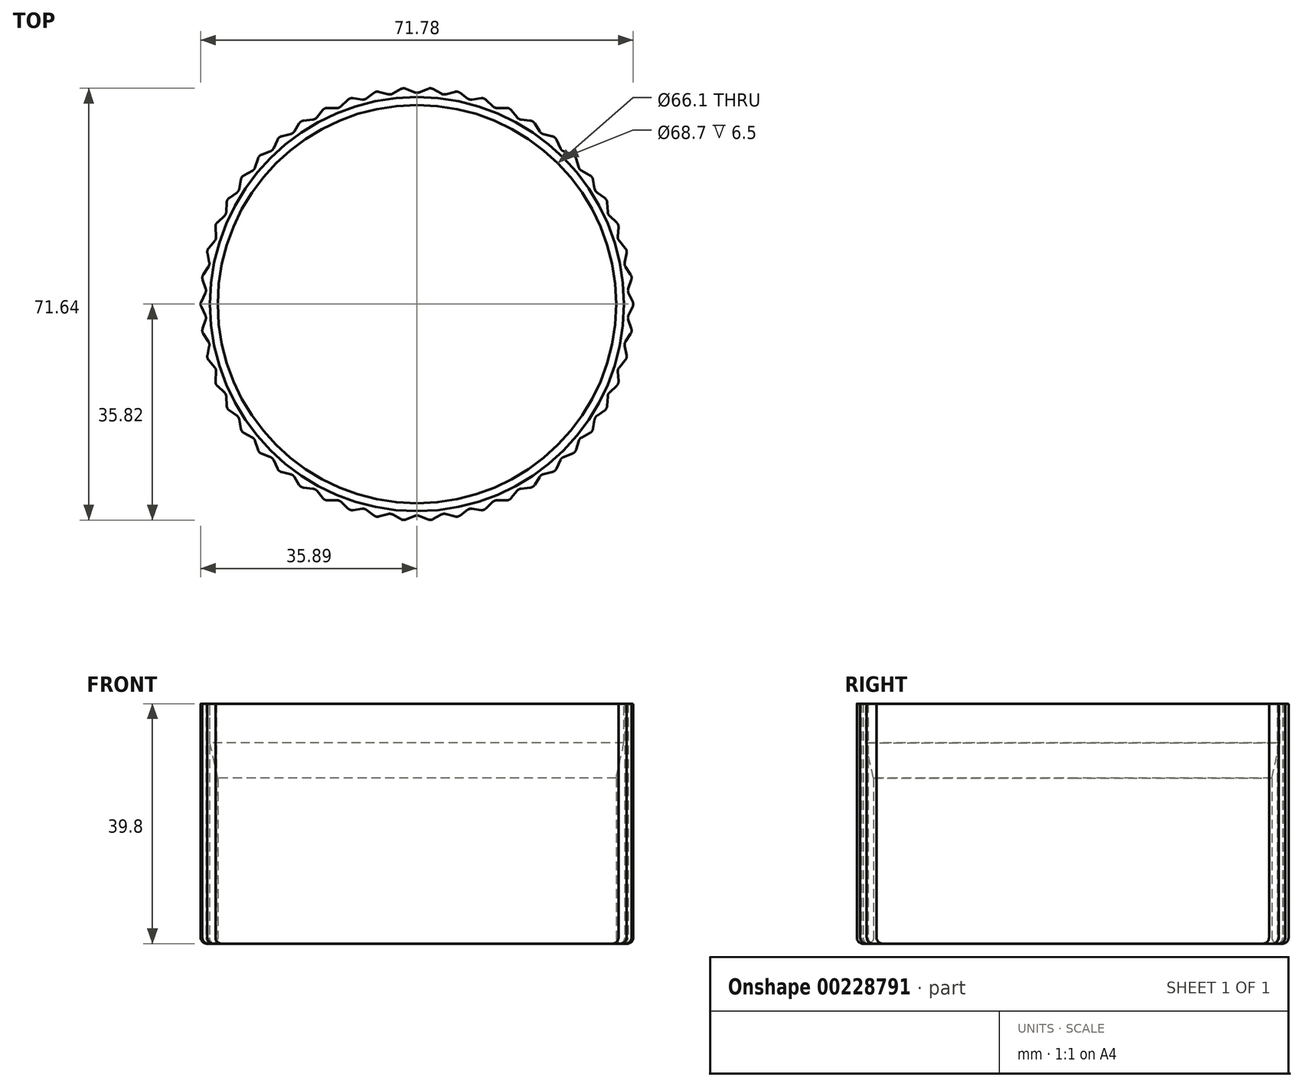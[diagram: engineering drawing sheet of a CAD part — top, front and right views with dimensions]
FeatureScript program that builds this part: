
annotation { "Feature Type Name" : "Feature", "Feature Type Description" : "" }
export const myFeature = defineFeature(function(context is Context, id is Id, definition is map)
    precondition{}
    {
        {
            var Q0;
            Q0=qCreatedBy(makeId("Top.planeOp"),FACE);
            var sketch = newSketch(context, id + "F0", { "sketchPlane" : qUnion([Q0])});
            skCircle(sketch, "E0", {"center": v(0, 0) * mm, "radius": 33.05 * mm});
            skLineSegment(sketch, "E1", {"start": v(2.68, 35.69) * mm, "end": v(4.03, 34.93) * mm});
            skLineSegment(sketch, "E2", {"start": v(4.78, 34.83) * mm, "end": v(6.28, 35.24) * mm});
            skPoint(sketch, "E3.visualSharp", {"position": v(2.26, 35.93) * mm});
            skArc(sketch, "E3.filletArc", {"start": v(2.68, 35.69) * mm, "mid": v(2.25, 35.82) * mm, "end": v(1.81, 35.74) * mm});
            skPoint(sketch, "E4.visualSharp", {"position": v(4.39, 34.72) * mm});
            skArc(sketch, "E4.filletArc", {"start": v(4.03, 34.93) * mm, "mid": v(4.4, 34.8) * mm, "end": v(4.78, 34.83) * mm});
            skPoint(sketch, "E5.visualSharp", {"position": v(6.75, 35.36) * mm});
            skArc(sketch, "E5.filletArc", {"start": v(6.72, 35.25) * mm, "mid": v(6.5, 35.27) * mm, "end": v(6.28, 35.24) * mm});
            skLineSegment(sketch, "E6.1.0", {"start": v(-1.81, 35.74) * mm, "end": v(-0.38, 35.16) * mm});
            skPoint(sketch, "E6.1.1", {"position": v(0, 35) * mm});
            skPoint(sketch, "E6.1.2", {"position": v(-2.26, 35.93) * mm});
            skArc(sketch, "E6.1.4", {"start": v(-0.38, 35.16) * mm, "mid": v(0, 35.08) * mm, "end": v(0.38, 35.16) * mm});
            skLineSegment(sketch, "E6.1.5", {"start": v(0.38, 35.16) * mm, "end": v(1.81, 35.74) * mm});
            skArc(sketch, "E6.1.6", {"start": v(-1.81, 35.74) * mm, "mid": v(-2.25, 35.82) * mm, "end": v(-2.68, 35.69) * mm});
            skArc(sketch, "E6.1.7", {"start": v(2.25, 35.82) * mm, "mid": v(2.03, 35.8) * mm, "end": v(1.81, 35.74) * mm});
            skLineSegment(sketch, "E6.2.0", {"start": v(-6.28, 35.24) * mm, "end": v(-4.78, 34.83) * mm});
            skPoint(sketch, "E6.2.1", {"position": v(-4.39, 34.72) * mm});
            skPoint(sketch, "E6.2.2", {"position": v(-6.75, 35.36) * mm});
            skPoint(sketch, "E6.2.3", {"position": v(-2.26, 35.93) * mm});
            skArc(sketch, "E6.2.4", {"start": v(-4.78, 34.83) * mm, "mid": v(-4.4, 34.8) * mm, "end": v(-4.03, 34.93) * mm});
            skLineSegment(sketch, "E6.2.5", {"start": v(-4.03, 34.93) * mm, "end": v(-2.68, 35.69) * mm});
            skArc(sketch, "E6.2.6", {"start": v(-6.28, 35.24) * mm, "mid": v(-6.72, 35.25) * mm, "end": v(-7.14, 35.07) * mm});
            skArc(sketch, "E6.2.7", {"start": v(-2.25, 35.82) * mm, "mid": v(-2.48, 35.78) * mm, "end": v(-2.68, 35.69) * mm});
            skLineSegment(sketch, "E6.3.0", {"start": v(-10.64, 34.17) * mm, "end": v(-9.11, 33.96) * mm});
            skPoint(sketch, "E6.3.1", {"position": v(-8.7, 33.9) * mm});
            skPoint(sketch, "E6.3.2", {"position": v(-11.12, 34.24) * mm});
            skPoint(sketch, "E6.3.3", {"position": v(-6.75, 35.36) * mm});
            skArc(sketch, "E6.3.4", {"start": v(-9.11, 33.96) * mm, "mid": v(-8.72, 33.98) * mm, "end": v(-8.37, 34.15) * mm});
            skLineSegment(sketch, "E6.3.5", {"start": v(-8.37, 34.15) * mm, "end": v(-7.14, 35.07) * mm});
            skArc(sketch, "E6.3.6", {"start": v(-10.64, 34.17) * mm, "mid": v(-11.09, 34.13) * mm, "end": v(-11.47, 33.9) * mm});
            skArc(sketch, "E6.3.7", {"start": v(-6.72, 35.25) * mm, "mid": v(-6.94, 35.19) * mm, "end": v(-7.14, 35.07) * mm});
            skLineSegment(sketch, "E6.4.0", {"start": v(-14.84, 32.57) * mm, "end": v(-13.3, 32.55) * mm});
            skPoint(sketch, "E6.4.1", {"position": v(-12.88, 32.54) * mm});
            skPoint(sketch, "E6.4.2", {"position": v(-15.33, 32.57) * mm});
            skPoint(sketch, "E6.4.3", {"position": v(-11.12, 34.24) * mm});
            skArc(sketch, "E6.4.4", {"start": v(-13.3, 32.55) * mm, "mid": v(-12.91, 32.62) * mm, "end": v(-12.59, 32.83) * mm});
            skLineSegment(sketch, "E6.4.5", {"start": v(-12.59, 32.83) * mm, "end": v(-11.47, 33.9) * mm});
            skArc(sketch, "E6.4.6", {"start": v(-14.84, 32.57) * mm, "mid": v(-15.28, 32.47) * mm, "end": v(-15.63, 32.2) * mm});
            skArc(sketch, "E6.4.7", {"start": v(-11.09, 34.13) * mm, "mid": v(-11.3, 34.04) * mm, "end": v(-11.47, 33.9) * mm});
            skLineSegment(sketch, "E6.5.0", {"start": v(-18.8, 30.45) * mm, "end": v(-17.27, 30.62) * mm});
            skPoint(sketch, "E6.5.1", {"position": v(-16.86, 30.67) * mm});
            skPoint(sketch, "E6.5.2", {"position": v(-19.29, 30.4) * mm});
            skPoint(sketch, "E6.5.3", {"position": v(-15.33, 32.57) * mm});
            skArc(sketch, "E6.5.4", {"start": v(-17.27, 30.62) * mm, "mid": v(-16.9, 30.74) * mm, "end": v(-16.6, 31) * mm});
            skLineSegment(sketch, "E6.5.5", {"start": v(-16.6, 31) * mm, "end": v(-15.63, 32.2) * mm});
            skArc(sketch, "E6.5.6", {"start": v(-18.8, 30.45) * mm, "mid": v(-19.23, 30.3) * mm, "end": v(-19.55, 29.98) * mm});
            skArc(sketch, "E6.5.7", {"start": v(-15.28, 32.47) * mm, "mid": v(-15.47, 32.35) * mm, "end": v(-15.63, 32.2) * mm});
            skLineSegment(sketch, "E6.6.0", {"start": v(-22.47, 27.85) * mm, "end": v(-20.97, 28.22) * mm});
            skPoint(sketch, "E6.6.1", {"position": v(-20.57, 28.32) * mm});
            skPoint(sketch, "E6.6.2", {"position": v(-22.95, 27.74) * mm});
            skPoint(sketch, "E6.6.3", {"position": v(-19.29, 30.4) * mm});
            skArc(sketch, "E6.6.4", {"start": v(-20.97, 28.22) * mm, "mid": v(-20.62, 28.38) * mm, "end": v(-20.36, 28.67) * mm});
            skLineSegment(sketch, "E6.6.5", {"start": v(-20.36, 28.67) * mm, "end": v(-19.55, 29.98) * mm});
            skArc(sketch, "E6.6.6", {"start": v(-22.47, 27.85) * mm, "mid": v(-22.88, 27.65) * mm, "end": v(-23.15, 27.3) * mm});
            skArc(sketch, "E6.6.7", {"start": v(-19.23, 30.3) * mm, "mid": v(-19.4, 30.16) * mm, "end": v(-19.55, 29.98) * mm});
            skLineSegment(sketch, "E6.7.0", {"start": v(-25.79, 24.82) * mm, "end": v(-24.34, 25.37) * mm});
            skPoint(sketch, "E6.7.1", {"position": v(-23.96, 25.51) * mm});
            skPoint(sketch, "E6.7.2", {"position": v(-26.24, 24.64) * mm});
            skPoint(sketch, "E6.7.3", {"position": v(-22.95, 27.74) * mm});
            skArc(sketch, "E6.7.4", {"start": v(-24.34, 25.37) * mm, "mid": v(-24.01, 25.57) * mm, "end": v(-23.79, 25.89) * mm});
            skLineSegment(sketch, "E6.7.5", {"start": v(-23.79, 25.89) * mm, "end": v(-23.15, 27.3) * mm});
            skArc(sketch, "E6.7.6", {"start": v(-25.79, 24.82) * mm, "mid": v(-26.16, 24.57) * mm, "end": v(-26.39, 24.18) * mm});
            skArc(sketch, "E6.7.7", {"start": v(-22.88, 27.65) * mm, "mid": v(-23.03, 27.49) * mm, "end": v(-23.15, 27.3) * mm});
            skLineSegment(sketch, "E6.8.0", {"start": v(-28.7, 21.39) * mm, "end": v(-27.33, 22.12) * mm});
            skPoint(sketch, "E6.8.1", {"position": v(-26.97, 22.3) * mm});
            skPoint(sketch, "E6.8.2", {"position": v(-29.12, 21.16) * mm});
            skPoint(sketch, "E6.8.3", {"position": v(-26.24, 24.64) * mm});
            skArc(sketch, "E6.8.4", {"start": v(-27.33, 22.12) * mm, "mid": v(-27.03, 22.36) * mm, "end": v(-26.85, 22.7) * mm});
            skLineSegment(sketch, "E6.8.5", {"start": v(-26.85, 22.7) * mm, "end": v(-26.39, 24.18) * mm});
            skArc(sketch, "E6.8.6", {"start": v(-28.7, 21.39) * mm, "mid": v(-29.03, 21.1) * mm, "end": v(-29.2, 20.68) * mm});
            skArc(sketch, "E6.8.7", {"start": v(-26.16, 24.57) * mm, "mid": v(-26.3, 24.39) * mm, "end": v(-26.39, 24.18) * mm});
            skLineSegment(sketch, "E6.9.0", {"start": v(-31.15, 17.62) * mm, "end": v(-29.89, 18.52) * mm});
            skPoint(sketch, "E6.9.1", {"position": v(-29.55, 18.75) * mm});
            skPoint(sketch, "E6.9.2", {"position": v(-31.55, 17.34) * mm});
            skPoint(sketch, "E6.9.3", {"position": v(-29.12, 21.16) * mm});
            skArc(sketch, "E6.9.4", {"start": v(-29.89, 18.52) * mm, "mid": v(-29.62, 18.8) * mm, "end": v(-29.48, 19.16) * mm});
            skLineSegment(sketch, "E6.9.5", {"start": v(-29.48, 19.16) * mm, "end": v(-29.2, 20.68) * mm});
            skArc(sketch, "E6.9.6", {"start": v(-31.15, 17.62) * mm, "mid": v(-31.45, 17.29) * mm, "end": v(-31.57, 16.86) * mm});
            skArc(sketch, "E6.9.7", {"start": v(-29.03, 21.1) * mm, "mid": v(-29.15, 20.9) * mm, "end": v(-29.2, 20.68) * mm});
            skLineSegment(sketch, "E6.10.0", {"start": v(-33.11, 13.58) * mm, "end": v(-31.97, 14.62) * mm});
            skPoint(sketch, "E6.10.1", {"position": v(-31.67, 14.9) * mm});
            skPoint(sketch, "E6.10.2", {"position": v(-33.47, 13.25) * mm});
            skPoint(sketch, "E6.10.3", {"position": v(-31.55, 17.34) * mm});
            skArc(sketch, "E6.10.4", {"start": v(-31.97, 14.62) * mm, "mid": v(-31.74, 14.94) * mm, "end": v(-31.65, 15.31) * mm});
            skLineSegment(sketch, "E6.10.5", {"start": v(-31.65, 15.31) * mm, "end": v(-31.57, 16.86) * mm});
            skArc(sketch, "E6.10.6", {"start": v(-33.11, 13.58) * mm, "mid": v(-33.37, 13.21) * mm, "end": v(-33.44, 12.77) * mm});
            skArc(sketch, "E6.10.7", {"start": v(-31.45, 17.29) * mm, "mid": v(-31.53, 17.08) * mm, "end": v(-31.57, 16.86) * mm});
            skLineSegment(sketch, "E6.11.0", {"start": v(-34.55, 9.32) * mm, "end": v(-33.55, 10.5) * mm});
            skPoint(sketch, "E6.11.1", {"position": v(-33.29, 10.82) * mm});
            skPoint(sketch, "E6.11.2", {"position": v(-34.87, 8.95) * mm});
            skPoint(sketch, "E6.11.3", {"position": v(-33.47, 13.25) * mm});
            skArc(sketch, "E6.11.4", {"start": v(-33.55, 10.5) * mm, "mid": v(-33.36, 10.84) * mm, "end": v(-33.32, 11.23) * mm});
            skLineSegment(sketch, "E6.11.5", {"start": v(-33.32, 11.23) * mm, "end": v(-33.44, 12.77) * mm});
            skArc(sketch, "E6.11.6", {"start": v(-34.55, 9.32) * mm, "mid": v(-34.76, 8.92) * mm, "end": v(-34.77, 8.48) * mm});
            skArc(sketch, "E6.11.7", {"start": v(-33.37, 13.21) * mm, "mid": v(-33.43, 13) * mm, "end": v(-33.44, 12.77) * mm});
            skLineSegment(sketch, "E6.12.0", {"start": v(-35.45, 4.92) * mm, "end": v(-34.6, 6.21) * mm});
            skPoint(sketch, "E6.12.1", {"position": v(-34.38, 6.56) * mm});
            skPoint(sketch, "E6.12.2", {"position": v(-35.72, 4.51) * mm});
            skPoint(sketch, "E6.12.3", {"position": v(-34.87, 8.95) * mm});
            skArc(sketch, "E6.12.4", {"start": v(-34.6, 6.21) * mm, "mid": v(-34.46, 6.57) * mm, "end": v(-34.46, 6.96) * mm});
            skLineSegment(sketch, "E6.12.5", {"start": v(-34.46, 6.96) * mm, "end": v(-34.77, 8.48) * mm});
            skArc(sketch, "E6.12.6", {"start": v(-35.45, 4.92) * mm, "mid": v(-35.6, 4.5) * mm, "end": v(-35.56, 4.05) * mm});
            skArc(sketch, "E6.12.7", {"start": v(-34.76, 8.92) * mm, "mid": v(-34.8, 8.7) * mm, "end": v(-34.77, 8.48) * mm});
            skLineSegment(sketch, "E6.13.0", {"start": v(-35.79, 0.44) * mm, "end": v(-35.11, 1.83) * mm});
            skPoint(sketch, "E6.13.1", {"position": v(-34.93, 2.2) * mm});
            skPoint(sketch, "E6.13.2", {"position": v(-36, 0) * mm});
            skPoint(sketch, "E6.13.3", {"position": v(-35.72, 4.51) * mm});
            skArc(sketch, "E6.13.4", {"start": v(-35.11, 1.83) * mm, "mid": v(-35.01, 2.2) * mm, "end": v(-35.06, 2.59) * mm});
            skLineSegment(sketch, "E6.13.5", {"start": v(-35.06, 2.59) * mm, "end": v(-35.56, 4.05) * mm});
            skArc(sketch, "E6.13.6", {"start": v(-35.79, 0.44) * mm, "mid": v(-35.89, 0) * mm, "end": v(-35.79, -0.44) * mm});
            skArc(sketch, "E6.13.7", {"start": v(-35.6, 4.5) * mm, "mid": v(-35.6, 4.27) * mm, "end": v(-35.56, 4.05) * mm});
            skLineSegment(sketch, "E6.14.0", {"start": v(-35.56, -4.05) * mm, "end": v(-35.06, -2.59) * mm});
            skPoint(sketch, "E6.14.1", {"position": v(-34.93, -2.2) * mm});
            skPoint(sketch, "E6.14.2", {"position": v(-35.72, -4.51) * mm});
            skPoint(sketch, "E6.14.3", {"position": v(-36, 0) * mm});
            skArc(sketch, "E6.14.4", {"start": v(-35.06, -2.59) * mm, "mid": v(-35.01, -2.2) * mm, "end": v(-35.11, -1.83) * mm});
            skLineSegment(sketch, "E6.14.5", {"start": v(-35.11, -1.83) * mm, "end": v(-35.79, -0.44) * mm});
            skArc(sketch, "E6.14.6", {"start": v(-35.56, -4.05) * mm, "mid": v(-35.6, -4.5) * mm, "end": v(-35.45, -4.92) * mm});
            skArc(sketch, "E6.14.7", {"start": v(-35.89, 0) * mm, "mid": v(-35.86, -0.22) * mm, "end": v(-35.79, -0.44) * mm});
            skLineSegment(sketch, "E6.15.0", {"start": v(-34.77, -8.48) * mm, "end": v(-34.46, -6.96) * mm});
            skPoint(sketch, "E6.15.1", {"position": v(-34.38, -6.56) * mm});
            skPoint(sketch, "E6.15.2", {"position": v(-34.87, -8.95) * mm});
            skPoint(sketch, "E6.15.3", {"position": v(-35.72, -4.51) * mm});
            skArc(sketch, "E6.15.4", {"start": v(-34.46, -6.96) * mm, "mid": v(-34.46, -6.57) * mm, "end": v(-34.6, -6.21) * mm});
            skLineSegment(sketch, "E6.15.5", {"start": v(-34.6, -6.21) * mm, "end": v(-35.45, -4.92) * mm});
            skArc(sketch, "E6.15.6", {"start": v(-34.77, -8.48) * mm, "mid": v(-34.76, -8.92) * mm, "end": v(-34.55, -9.32) * mm});
            skArc(sketch, "E6.15.7", {"start": v(-35.6, -4.5) * mm, "mid": v(-35.55, -4.72) * mm, "end": v(-35.45, -4.92) * mm});
            skLineSegment(sketch, "E6.16.0", {"start": v(-33.44, -12.77) * mm, "end": v(-33.32, -11.23) * mm});
            skPoint(sketch, "E6.16.1", {"position": v(-33.29, -10.82) * mm});
            skPoint(sketch, "E6.16.2", {"position": v(-33.47, -13.25) * mm});
            skPoint(sketch, "E6.16.3", {"position": v(-34.87, -8.95) * mm});
            skArc(sketch, "E6.16.4", {"start": v(-33.32, -11.23) * mm, "mid": v(-33.36, -10.84) * mm, "end": v(-33.55, -10.5) * mm});
            skLineSegment(sketch, "E6.16.5", {"start": v(-33.55, -10.5) * mm, "end": v(-34.55, -9.32) * mm});
            skArc(sketch, "E6.16.6", {"start": v(-33.44, -12.77) * mm, "mid": v(-33.37, -13.21) * mm, "end": v(-33.11, -13.58) * mm});
            skArc(sketch, "E6.16.7", {"start": v(-34.76, -8.92) * mm, "mid": v(-34.68, -9.14) * mm, "end": v(-34.55, -9.32) * mm});
            skLineSegment(sketch, "E6.17.0", {"start": v(-31.57, -16.86) * mm, "end": v(-31.65, -15.31) * mm});
            skPoint(sketch, "E6.17.1", {"position": v(-31.67, -14.9) * mm});
            skPoint(sketch, "E6.17.2", {"position": v(-31.55, -17.34) * mm});
            skPoint(sketch, "E6.17.3", {"position": v(-33.47, -13.25) * mm});
            skArc(sketch, "E6.17.4", {"start": v(-31.65, -15.31) * mm, "mid": v(-31.74, -14.94) * mm, "end": v(-31.97, -14.62) * mm});
            skLineSegment(sketch, "E6.17.5", {"start": v(-31.97, -14.62) * mm, "end": v(-33.11, -13.58) * mm});
            skArc(sketch, "E6.17.6", {"start": v(-31.57, -16.86) * mm, "mid": v(-31.45, -17.29) * mm, "end": v(-31.15, -17.62) * mm});
            skArc(sketch, "E6.17.7", {"start": v(-33.37, -13.21) * mm, "mid": v(-33.26, -13.41) * mm, "end": v(-33.11, -13.58) * mm});
            skLineSegment(sketch, "E6.18.0", {"start": v(-29.2, -20.68) * mm, "end": v(-29.48, -19.16) * mm});
            skPoint(sketch, "E6.18.1", {"position": v(-29.55, -18.75) * mm});
            skPoint(sketch, "E6.18.2", {"position": v(-29.12, -21.16) * mm});
            skPoint(sketch, "E6.18.3", {"position": v(-31.55, -17.34) * mm});
            skArc(sketch, "E6.18.4", {"start": v(-29.48, -19.16) * mm, "mid": v(-29.62, -18.8) * mm, "end": v(-29.89, -18.52) * mm});
            skLineSegment(sketch, "E6.18.5", {"start": v(-29.89, -18.52) * mm, "end": v(-31.15, -17.62) * mm});
            skArc(sketch, "E6.18.6", {"start": v(-29.2, -20.68) * mm, "mid": v(-29.03, -21.1) * mm, "end": v(-28.7, -21.39) * mm});
            skArc(sketch, "E6.18.7", {"start": v(-31.45, -17.29) * mm, "mid": v(-31.32, -17.47) * mm, "end": v(-31.15, -17.62) * mm});
            skLineSegment(sketch, "E6.19.0", {"start": v(-26.39, -24.18) * mm, "end": v(-26.85, -22.7) * mm});
            skPoint(sketch, "E6.19.1", {"position": v(-26.97, -22.3) * mm});
            skPoint(sketch, "E6.19.2", {"position": v(-26.24, -24.64) * mm});
            skPoint(sketch, "E6.19.3", {"position": v(-29.12, -21.16) * mm});
            skArc(sketch, "E6.19.4", {"start": v(-26.85, -22.7) * mm, "mid": v(-27.03, -22.36) * mm, "end": v(-27.33, -22.12) * mm});
            skLineSegment(sketch, "E6.19.5", {"start": v(-27.33, -22.12) * mm, "end": v(-28.7, -21.39) * mm});
            skArc(sketch, "E6.19.6", {"start": v(-26.39, -24.18) * mm, "mid": v(-26.16, -24.57) * mm, "end": v(-25.79, -24.82) * mm});
            skArc(sketch, "E6.19.7", {"start": v(-29.03, -21.1) * mm, "mid": v(-28.88, -21.26) * mm, "end": v(-28.7, -21.39) * mm});
            skLineSegment(sketch, "E6.20.0", {"start": v(-23.15, -27.3) * mm, "end": v(-23.79, -25.89) * mm});
            skPoint(sketch, "E6.20.1", {"position": v(-23.96, -25.51) * mm});
            skPoint(sketch, "E6.20.2", {"position": v(-22.95, -27.74) * mm});
            skPoint(sketch, "E6.20.3", {"position": v(-26.24, -24.64) * mm});
            skArc(sketch, "E6.20.4", {"start": v(-23.79, -25.89) * mm, "mid": v(-24.01, -25.57) * mm, "end": v(-24.34, -25.37) * mm});
            skLineSegment(sketch, "E6.20.5", {"start": v(-24.34, -25.37) * mm, "end": v(-25.79, -24.82) * mm});
            skArc(sketch, "E6.20.6", {"start": v(-23.15, -27.3) * mm, "mid": v(-22.88, -27.65) * mm, "end": v(-22.47, -27.85) * mm});
            skArc(sketch, "E6.20.7", {"start": v(-26.16, -24.57) * mm, "mid": v(-25.99, -24.71) * mm, "end": v(-25.79, -24.82) * mm});
            skLineSegment(sketch, "E6.21.0", {"start": v(-19.55, -29.98) * mm, "end": v(-20.36, -28.67) * mm});
            skPoint(sketch, "E6.21.1", {"position": v(-20.57, -28.32) * mm});
            skPoint(sketch, "E6.21.2", {"position": v(-19.29, -30.4) * mm});
            skPoint(sketch, "E6.21.3", {"position": v(-22.95, -27.74) * mm});
            skArc(sketch, "E6.21.4", {"start": v(-20.36, -28.67) * mm, "mid": v(-20.62, -28.38) * mm, "end": v(-20.97, -28.22) * mm});
            skLineSegment(sketch, "E6.21.5", {"start": v(-20.97, -28.22) * mm, "end": v(-22.47, -27.85) * mm});
            skArc(sketch, "E6.21.6", {"start": v(-19.55, -29.98) * mm, "mid": v(-19.23, -30.3) * mm, "end": v(-18.8, -30.45) * mm});
            skArc(sketch, "E6.21.7", {"start": v(-22.88, -27.65) * mm, "mid": v(-22.69, -27.78) * mm, "end": v(-22.47, -27.85) * mm});
            skLineSegment(sketch, "E6.22.0", {"start": v(-15.63, -32.2) * mm, "end": v(-16.6, -31) * mm});
            skPoint(sketch, "E6.22.1", {"position": v(-16.86, -30.67) * mm});
            skPoint(sketch, "E6.22.2", {"position": v(-15.33, -32.57) * mm});
            skPoint(sketch, "E6.22.3", {"position": v(-19.29, -30.4) * mm});
            skArc(sketch, "E6.22.4", {"start": v(-16.6, -31) * mm, "mid": v(-16.9, -30.74) * mm, "end": v(-17.27, -30.62) * mm});
            skLineSegment(sketch, "E6.22.5", {"start": v(-17.27, -30.62) * mm, "end": v(-18.8, -30.45) * mm});
            skArc(sketch, "E6.22.6", {"start": v(-15.63, -32.2) * mm, "mid": v(-15.28, -32.47) * mm, "end": v(-14.84, -32.57) * mm});
            skArc(sketch, "E6.22.7", {"start": v(-19.23, -30.3) * mm, "mid": v(-19.03, -30.4) * mm, "end": v(-18.8, -30.45) * mm});
            skLineSegment(sketch, "E6.23.0", {"start": v(-11.47, -33.9) * mm, "end": v(-12.59, -32.83) * mm});
            skPoint(sketch, "E6.23.1", {"position": v(-12.88, -32.54) * mm});
            skPoint(sketch, "E6.23.2", {"position": v(-11.12, -34.24) * mm});
            skPoint(sketch, "E6.23.3", {"position": v(-15.33, -32.57) * mm});
            skArc(sketch, "E6.23.4", {"start": v(-12.59, -32.83) * mm, "mid": v(-12.91, -32.62) * mm, "end": v(-13.3, -32.55) * mm});
            skLineSegment(sketch, "E6.23.5", {"start": v(-13.3, -32.55) * mm, "end": v(-14.84, -32.57) * mm});
            skArc(sketch, "E6.23.6", {"start": v(-11.47, -33.9) * mm, "mid": v(-11.09, -34.13) * mm, "end": v(-10.64, -34.17) * mm});
            skArc(sketch, "E6.23.7", {"start": v(-15.28, -32.47) * mm, "mid": v(-15.07, -32.54) * mm, "end": v(-14.84, -32.57) * mm});
            skLineSegment(sketch, "E6.24.0", {"start": v(-7.14, -35.07) * mm, "end": v(-8.37, -34.15) * mm});
            skPoint(sketch, "E6.24.1", {"position": v(-8.7, -33.9) * mm});
            skPoint(sketch, "E6.24.2", {"position": v(-6.75, -35.36) * mm});
            skPoint(sketch, "E6.24.3", {"position": v(-11.12, -34.24) * mm});
            skArc(sketch, "E6.24.4", {"start": v(-8.37, -34.15) * mm, "mid": v(-8.72, -33.98) * mm, "end": v(-9.11, -33.96) * mm});
            skLineSegment(sketch, "E6.24.5", {"start": v(-9.11, -33.96) * mm, "end": v(-10.64, -34.17) * mm});
            skArc(sketch, "E6.24.6", {"start": v(-7.14, -35.07) * mm, "mid": v(-6.72, -35.25) * mm, "end": v(-6.28, -35.24) * mm});
            skArc(sketch, "E6.24.7", {"start": v(-11.09, -34.13) * mm, "mid": v(-10.87, -34.18) * mm, "end": v(-10.64, -34.17) * mm});
            skLineSegment(sketch, "E6.25.0", {"start": v(-2.68, -35.69) * mm, "end": v(-4.03, -34.93) * mm});
            skPoint(sketch, "E6.25.1", {"position": v(-4.39, -34.72) * mm});
            skPoint(sketch, "E6.25.2", {"position": v(-2.26, -35.93) * mm});
            skPoint(sketch, "E6.25.3", {"position": v(-6.75, -35.36) * mm});
            skArc(sketch, "E6.25.4", {"start": v(-4.03, -34.93) * mm, "mid": v(-4.4, -34.8) * mm, "end": v(-4.78, -34.83) * mm});
            skLineSegment(sketch, "E6.25.5", {"start": v(-4.78, -34.83) * mm, "end": v(-6.28, -35.24) * mm});
            skArc(sketch, "E6.25.6", {"start": v(-2.68, -35.69) * mm, "mid": v(-2.25, -35.82) * mm, "end": v(-1.81, -35.74) * mm});
            skArc(sketch, "E6.25.7", {"start": v(-6.72, -35.25) * mm, "mid": v(-6.5, -35.27) * mm, "end": v(-6.28, -35.24) * mm});
            skLineSegment(sketch, "E6.26.0", {"start": v(1.81, -35.74) * mm, "end": v(0.38, -35.16) * mm});
            skPoint(sketch, "E6.26.1", {"position": v(0, -35) * mm});
            skPoint(sketch, "E6.26.2", {"position": v(2.26, -35.93) * mm});
            skPoint(sketch, "E6.26.3", {"position": v(-2.26, -35.93) * mm});
            skArc(sketch, "E6.26.4", {"start": v(0.38, -35.16) * mm, "mid": v(0, -35.08) * mm, "end": v(-0.38, -35.16) * mm});
            skLineSegment(sketch, "E6.26.5", {"start": v(-0.38, -35.16) * mm, "end": v(-1.81, -35.74) * mm});
            skArc(sketch, "E6.26.6", {"start": v(1.81, -35.74) * mm, "mid": v(2.25, -35.82) * mm, "end": v(2.68, -35.69) * mm});
            skArc(sketch, "E6.26.7", {"start": v(-2.25, -35.82) * mm, "mid": v(-2.03, -35.8) * mm, "end": v(-1.81, -35.74) * mm});
            skLineSegment(sketch, "E6.27.0", {"start": v(6.28, -35.24) * mm, "end": v(4.78, -34.83) * mm});
            skPoint(sketch, "E6.27.1", {"position": v(4.39, -34.72) * mm});
            skPoint(sketch, "E6.27.2", {"position": v(6.75, -35.36) * mm});
            skPoint(sketch, "E6.27.3", {"position": v(2.26, -35.93) * mm});
            skArc(sketch, "E6.27.4", {"start": v(4.78, -34.83) * mm, "mid": v(4.4, -34.8) * mm, "end": v(4.03, -34.93) * mm});
            skLineSegment(sketch, "E6.27.5", {"start": v(4.03, -34.93) * mm, "end": v(2.68, -35.69) * mm});
            skArc(sketch, "E6.27.6", {"start": v(6.28, -35.24) * mm, "mid": v(6.72, -35.25) * mm, "end": v(7.14, -35.07) * mm});
            skArc(sketch, "E6.27.7", {"start": v(2.25, -35.82) * mm, "mid": v(2.48, -35.78) * mm, "end": v(2.68, -35.69) * mm});
            skLineSegment(sketch, "E6.28.0", {"start": v(10.64, -34.17) * mm, "end": v(9.11, -33.96) * mm});
            skPoint(sketch, "E6.28.1", {"position": v(8.7, -33.9) * mm});
            skPoint(sketch, "E6.28.2", {"position": v(11.12, -34.24) * mm});
            skPoint(sketch, "E6.28.3", {"position": v(6.75, -35.36) * mm});
            skArc(sketch, "E6.28.4", {"start": v(9.11, -33.96) * mm, "mid": v(8.72, -33.98) * mm, "end": v(8.37, -34.15) * mm});
            skLineSegment(sketch, "E6.28.5", {"start": v(8.37, -34.15) * mm, "end": v(7.14, -35.07) * mm});
            skArc(sketch, "E6.28.6", {"start": v(10.64, -34.17) * mm, "mid": v(11.09, -34.13) * mm, "end": v(11.47, -33.9) * mm});
            skArc(sketch, "E6.28.7", {"start": v(6.72, -35.25) * mm, "mid": v(6.94, -35.19) * mm, "end": v(7.14, -35.07) * mm});
            skLineSegment(sketch, "E6.29.0", {"start": v(14.84, -32.57) * mm, "end": v(13.3, -32.55) * mm});
            skPoint(sketch, "E6.29.1", {"position": v(12.88, -32.54) * mm});
            skPoint(sketch, "E6.29.2", {"position": v(15.33, -32.57) * mm});
            skPoint(sketch, "E6.29.3", {"position": v(11.12, -34.24) * mm});
            skArc(sketch, "E6.29.4", {"start": v(13.3, -32.55) * mm, "mid": v(12.91, -32.62) * mm, "end": v(12.59, -32.83) * mm});
            skLineSegment(sketch, "E6.29.5", {"start": v(12.59, -32.83) * mm, "end": v(11.47, -33.9) * mm});
            skArc(sketch, "E6.29.6", {"start": v(14.84, -32.57) * mm, "mid": v(15.28, -32.47) * mm, "end": v(15.63, -32.2) * mm});
            skArc(sketch, "E6.29.7", {"start": v(11.09, -34.13) * mm, "mid": v(11.3, -34.04) * mm, "end": v(11.47, -33.9) * mm});
            skLineSegment(sketch, "E6.30.0", {"start": v(18.8, -30.45) * mm, "end": v(17.27, -30.62) * mm});
            skPoint(sketch, "E6.30.1", {"position": v(16.86, -30.67) * mm});
            skPoint(sketch, "E6.30.2", {"position": v(19.29, -30.4) * mm});
            skPoint(sketch, "E6.30.3", {"position": v(15.33, -32.57) * mm});
            skArc(sketch, "E6.30.4", {"start": v(17.27, -30.62) * mm, "mid": v(16.9, -30.74) * mm, "end": v(16.6, -31) * mm});
            skLineSegment(sketch, "E6.30.5", {"start": v(16.6, -31) * mm, "end": v(15.63, -32.2) * mm});
            skArc(sketch, "E6.30.6", {"start": v(18.8, -30.45) * mm, "mid": v(19.23, -30.3) * mm, "end": v(19.55, -29.98) * mm});
            skArc(sketch, "E6.30.7", {"start": v(15.28, -32.47) * mm, "mid": v(15.47, -32.35) * mm, "end": v(15.63, -32.2) * mm});
            skLineSegment(sketch, "E6.31.0", {"start": v(22.47, -27.85) * mm, "end": v(20.97, -28.22) * mm});
            skPoint(sketch, "E6.31.1", {"position": v(20.57, -28.32) * mm});
            skPoint(sketch, "E6.31.2", {"position": v(22.95, -27.74) * mm});
            skPoint(sketch, "E6.31.3", {"position": v(19.29, -30.4) * mm});
            skArc(sketch, "E6.31.4", {"start": v(20.97, -28.22) * mm, "mid": v(20.62, -28.38) * mm, "end": v(20.36, -28.67) * mm});
            skLineSegment(sketch, "E6.31.5", {"start": v(20.36, -28.67) * mm, "end": v(19.55, -29.98) * mm});
            skArc(sketch, "E6.31.6", {"start": v(22.47, -27.85) * mm, "mid": v(22.88, -27.65) * mm, "end": v(23.15, -27.3) * mm});
            skArc(sketch, "E6.31.7", {"start": v(19.23, -30.3) * mm, "mid": v(19.4, -30.16) * mm, "end": v(19.55, -29.98) * mm});
            skLineSegment(sketch, "E6.32.0", {"start": v(25.79, -24.82) * mm, "end": v(24.34, -25.37) * mm});
            skPoint(sketch, "E6.32.1", {"position": v(23.96, -25.51) * mm});
            skPoint(sketch, "E6.32.2", {"position": v(26.24, -24.64) * mm});
            skPoint(sketch, "E6.32.3", {"position": v(22.95, -27.74) * mm});
            skArc(sketch, "E6.32.4", {"start": v(24.34, -25.37) * mm, "mid": v(24.01, -25.57) * mm, "end": v(23.79, -25.89) * mm});
            skLineSegment(sketch, "E6.32.5", {"start": v(23.79, -25.89) * mm, "end": v(23.15, -27.3) * mm});
            skArc(sketch, "E6.32.6", {"start": v(25.79, -24.82) * mm, "mid": v(26.16, -24.57) * mm, "end": v(26.39, -24.18) * mm});
            skArc(sketch, "E6.32.7", {"start": v(22.88, -27.65) * mm, "mid": v(23.03, -27.49) * mm, "end": v(23.15, -27.3) * mm});
            skLineSegment(sketch, "E6.33.0", {"start": v(28.7, -21.39) * mm, "end": v(27.33, -22.12) * mm});
            skPoint(sketch, "E6.33.1", {"position": v(26.97, -22.3) * mm});
            skPoint(sketch, "E6.33.2", {"position": v(29.12, -21.16) * mm});
            skPoint(sketch, "E6.33.3", {"position": v(26.24, -24.64) * mm});
            skArc(sketch, "E6.33.4", {"start": v(27.33, -22.12) * mm, "mid": v(27.03, -22.36) * mm, "end": v(26.85, -22.7) * mm});
            skLineSegment(sketch, "E6.33.5", {"start": v(26.85, -22.7) * mm, "end": v(26.39, -24.18) * mm});
            skArc(sketch, "E6.33.6", {"start": v(28.7, -21.39) * mm, "mid": v(29.03, -21.1) * mm, "end": v(29.2, -20.68) * mm});
            skArc(sketch, "E6.33.7", {"start": v(26.16, -24.57) * mm, "mid": v(26.3, -24.39) * mm, "end": v(26.39, -24.18) * mm});
            skLineSegment(sketch, "E6.34.0", {"start": v(31.15, -17.62) * mm, "end": v(29.89, -18.52) * mm});
            skPoint(sketch, "E6.34.1", {"position": v(29.55, -18.75) * mm});
            skPoint(sketch, "E6.34.2", {"position": v(31.55, -17.34) * mm});
            skPoint(sketch, "E6.34.3", {"position": v(29.12, -21.16) * mm});
            skArc(sketch, "E6.34.4", {"start": v(29.89, -18.52) * mm, "mid": v(29.62, -18.8) * mm, "end": v(29.48, -19.16) * mm});
            skLineSegment(sketch, "E6.34.5", {"start": v(29.48, -19.16) * mm, "end": v(29.2, -20.68) * mm});
            skArc(sketch, "E6.34.6", {"start": v(31.15, -17.62) * mm, "mid": v(31.45, -17.29) * mm, "end": v(31.57, -16.86) * mm});
            skArc(sketch, "E6.34.7", {"start": v(29.03, -21.1) * mm, "mid": v(29.15, -20.9) * mm, "end": v(29.2, -20.68) * mm});
            skLineSegment(sketch, "E6.35.0", {"start": v(33.11, -13.58) * mm, "end": v(31.97, -14.62) * mm});
            skPoint(sketch, "E6.35.1", {"position": v(31.67, -14.9) * mm});
            skPoint(sketch, "E6.35.2", {"position": v(33.47, -13.25) * mm});
            skPoint(sketch, "E6.35.3", {"position": v(31.55, -17.34) * mm});
            skArc(sketch, "E6.35.4", {"start": v(31.97, -14.62) * mm, "mid": v(31.74, -14.94) * mm, "end": v(31.65, -15.31) * mm});
            skLineSegment(sketch, "E6.35.5", {"start": v(31.65, -15.31) * mm, "end": v(31.57, -16.86) * mm});
            skArc(sketch, "E6.35.6", {"start": v(33.11, -13.58) * mm, "mid": v(33.37, -13.21) * mm, "end": v(33.44, -12.77) * mm});
            skArc(sketch, "E6.35.7", {"start": v(31.45, -17.29) * mm, "mid": v(31.53, -17.08) * mm, "end": v(31.57, -16.86) * mm});
            skLineSegment(sketch, "E6.36.0", {"start": v(34.55, -9.32) * mm, "end": v(33.55, -10.5) * mm});
            skPoint(sketch, "E6.36.1", {"position": v(33.29, -10.82) * mm});
            skPoint(sketch, "E6.36.2", {"position": v(34.87, -8.95) * mm});
            skPoint(sketch, "E6.36.3", {"position": v(33.47, -13.25) * mm});
            skArc(sketch, "E6.36.4", {"start": v(33.55, -10.5) * mm, "mid": v(33.36, -10.84) * mm, "end": v(33.32, -11.23) * mm});
            skLineSegment(sketch, "E6.36.5", {"start": v(33.32, -11.23) * mm, "end": v(33.44, -12.77) * mm});
            skArc(sketch, "E6.36.6", {"start": v(34.55, -9.32) * mm, "mid": v(34.76, -8.92) * mm, "end": v(34.77, -8.48) * mm});
            skArc(sketch, "E6.36.7", {"start": v(33.37, -13.21) * mm, "mid": v(33.43, -13) * mm, "end": v(33.44, -12.77) * mm});
            skLineSegment(sketch, "E6.37.0", {"start": v(35.45, -4.92) * mm, "end": v(34.6, -6.21) * mm});
            skPoint(sketch, "E6.37.1", {"position": v(34.38, -6.56) * mm});
            skPoint(sketch, "E6.37.2", {"position": v(35.72, -4.51) * mm});
            skPoint(sketch, "E6.37.3", {"position": v(34.87, -8.95) * mm});
            skArc(sketch, "E6.37.4", {"start": v(34.6, -6.21) * mm, "mid": v(34.46, -6.57) * mm, "end": v(34.46, -6.96) * mm});
            skLineSegment(sketch, "E6.37.5", {"start": v(34.46, -6.96) * mm, "end": v(34.77, -8.48) * mm});
            skArc(sketch, "E6.37.6", {"start": v(35.45, -4.92) * mm, "mid": v(35.6, -4.5) * mm, "end": v(35.56, -4.05) * mm});
            skArc(sketch, "E6.37.7", {"start": v(34.76, -8.92) * mm, "mid": v(34.8, -8.7) * mm, "end": v(34.77, -8.48) * mm});
            skLineSegment(sketch, "E6.38.0", {"start": v(35.79, -0.44) * mm, "end": v(35.11, -1.83) * mm});
            skPoint(sketch, "E6.38.1", {"position": v(34.93, -2.2) * mm});
            skPoint(sketch, "E6.38.2", {"position": v(36, 0) * mm});
            skPoint(sketch, "E6.38.3", {"position": v(35.72, -4.51) * mm});
            skArc(sketch, "E6.38.4", {"start": v(35.11, -1.83) * mm, "mid": v(35.01, -2.2) * mm, "end": v(35.06, -2.59) * mm});
            skLineSegment(sketch, "E6.38.5", {"start": v(35.06, -2.59) * mm, "end": v(35.56, -4.05) * mm});
            skArc(sketch, "E6.38.6", {"start": v(35.79, -0.44) * mm, "mid": v(35.89, 0) * mm, "end": v(35.79, 0.44) * mm});
            skArc(sketch, "E6.38.7", {"start": v(35.6, -4.5) * mm, "mid": v(35.6, -4.27) * mm, "end": v(35.56, -4.05) * mm});
            skLineSegment(sketch, "E6.39.0", {"start": v(35.56, 4.05) * mm, "end": v(35.06, 2.59) * mm});
            skPoint(sketch, "E6.39.1", {"position": v(34.93, 2.2) * mm});
            skPoint(sketch, "E6.39.2", {"position": v(35.72, 4.51) * mm});
            skPoint(sketch, "E6.39.3", {"position": v(36, 0) * mm});
            skArc(sketch, "E6.39.4", {"start": v(35.06, 2.59) * mm, "mid": v(35.01, 2.2) * mm, "end": v(35.11, 1.83) * mm});
            skLineSegment(sketch, "E6.39.5", {"start": v(35.11, 1.83) * mm, "end": v(35.79, 0.44) * mm});
            skArc(sketch, "E6.39.6", {"start": v(35.56, 4.05) * mm, "mid": v(35.6, 4.5) * mm, "end": v(35.45, 4.92) * mm});
            skArc(sketch, "E6.39.7", {"start": v(35.89, 0) * mm, "mid": v(35.86, 0.22) * mm, "end": v(35.79, 0.44) * mm});
            skLineSegment(sketch, "E6.40.0", {"start": v(34.77, 8.48) * mm, "end": v(34.46, 6.96) * mm});
            skPoint(sketch, "E6.40.1", {"position": v(34.38, 6.56) * mm});
            skPoint(sketch, "E6.40.2", {"position": v(34.87, 8.95) * mm});
            skPoint(sketch, "E6.40.3", {"position": v(35.72, 4.51) * mm});
            skArc(sketch, "E6.40.4", {"start": v(34.46, 6.96) * mm, "mid": v(34.46, 6.57) * mm, "end": v(34.6, 6.21) * mm});
            skLineSegment(sketch, "E6.40.5", {"start": v(34.6, 6.21) * mm, "end": v(35.45, 4.92) * mm});
            skArc(sketch, "E6.40.6", {"start": v(34.77, 8.48) * mm, "mid": v(34.76, 8.92) * mm, "end": v(34.55, 9.32) * mm});
            skArc(sketch, "E6.40.7", {"start": v(35.6, 4.5) * mm, "mid": v(35.55, 4.72) * mm, "end": v(35.45, 4.92) * mm});
            skLineSegment(sketch, "E6.41.0", {"start": v(33.44, 12.77) * mm, "end": v(33.32, 11.23) * mm});
            skPoint(sketch, "E6.41.1", {"position": v(33.29, 10.82) * mm});
            skPoint(sketch, "E6.41.2", {"position": v(33.47, 13.25) * mm});
            skPoint(sketch, "E6.41.3", {"position": v(34.87, 8.95) * mm});
            skArc(sketch, "E6.41.4", {"start": v(33.32, 11.23) * mm, "mid": v(33.36, 10.84) * mm, "end": v(33.55, 10.5) * mm});
            skLineSegment(sketch, "E6.41.5", {"start": v(33.55, 10.5) * mm, "end": v(34.55, 9.32) * mm});
            skArc(sketch, "E6.41.6", {"start": v(33.44, 12.77) * mm, "mid": v(33.37, 13.21) * mm, "end": v(33.11, 13.58) * mm});
            skArc(sketch, "E6.41.7", {"start": v(34.76, 8.92) * mm, "mid": v(34.68, 9.14) * mm, "end": v(34.55, 9.32) * mm});
            skLineSegment(sketch, "E6.42.0", {"start": v(31.57, 16.86) * mm, "end": v(31.65, 15.31) * mm});
            skPoint(sketch, "E6.42.1", {"position": v(31.67, 14.9) * mm});
            skPoint(sketch, "E6.42.2", {"position": v(31.55, 17.34) * mm});
            skPoint(sketch, "E6.42.3", {"position": v(33.47, 13.25) * mm});
            skArc(sketch, "E6.42.4", {"start": v(31.65, 15.31) * mm, "mid": v(31.74, 14.94) * mm, "end": v(31.97, 14.62) * mm});
            skLineSegment(sketch, "E6.42.5", {"start": v(31.97, 14.62) * mm, "end": v(33.11, 13.58) * mm});
            skArc(sketch, "E6.42.6", {"start": v(31.57, 16.86) * mm, "mid": v(31.45, 17.29) * mm, "end": v(31.15, 17.62) * mm});
            skArc(sketch, "E6.42.7", {"start": v(33.37, 13.21) * mm, "mid": v(33.26, 13.41) * mm, "end": v(33.11, 13.58) * mm});
            skLineSegment(sketch, "E6.43.0", {"start": v(29.2, 20.68) * mm, "end": v(29.48, 19.16) * mm});
            skPoint(sketch, "E6.43.1", {"position": v(29.55, 18.75) * mm});
            skPoint(sketch, "E6.43.2", {"position": v(29.12, 21.16) * mm});
            skPoint(sketch, "E6.43.3", {"position": v(31.55, 17.34) * mm});
            skArc(sketch, "E6.43.4", {"start": v(29.48, 19.16) * mm, "mid": v(29.62, 18.8) * mm, "end": v(29.89, 18.52) * mm});
            skLineSegment(sketch, "E6.43.5", {"start": v(29.89, 18.52) * mm, "end": v(31.15, 17.62) * mm});
            skArc(sketch, "E6.43.6", {"start": v(29.2, 20.68) * mm, "mid": v(29.03, 21.1) * mm, "end": v(28.7, 21.39) * mm});
            skArc(sketch, "E6.43.7", {"start": v(31.45, 17.29) * mm, "mid": v(31.32, 17.47) * mm, "end": v(31.15, 17.62) * mm});
            skLineSegment(sketch, "E6.44.0", {"start": v(26.39, 24.18) * mm, "end": v(26.85, 22.7) * mm});
            skPoint(sketch, "E6.44.1", {"position": v(26.97, 22.3) * mm});
            skPoint(sketch, "E6.44.2", {"position": v(26.24, 24.64) * mm});
            skPoint(sketch, "E6.44.3", {"position": v(29.12, 21.16) * mm});
            skArc(sketch, "E6.44.4", {"start": v(26.85, 22.7) * mm, "mid": v(27.03, 22.36) * mm, "end": v(27.33, 22.12) * mm});
            skLineSegment(sketch, "E6.44.5", {"start": v(27.33, 22.12) * mm, "end": v(28.7, 21.39) * mm});
            skArc(sketch, "E6.44.6", {"start": v(26.39, 24.18) * mm, "mid": v(26.16, 24.57) * mm, "end": v(25.79, 24.82) * mm});
            skArc(sketch, "E6.44.7", {"start": v(29.03, 21.1) * mm, "mid": v(28.88, 21.26) * mm, "end": v(28.7, 21.39) * mm});
            skLineSegment(sketch, "E6.45.0", {"start": v(23.15, 27.3) * mm, "end": v(23.79, 25.89) * mm});
            skPoint(sketch, "E6.45.1", {"position": v(23.96, 25.51) * mm});
            skPoint(sketch, "E6.45.2", {"position": v(22.95, 27.74) * mm});
            skPoint(sketch, "E6.45.3", {"position": v(26.24, 24.64) * mm});
            skArc(sketch, "E6.45.4", {"start": v(23.79, 25.89) * mm, "mid": v(24.01, 25.57) * mm, "end": v(24.34, 25.37) * mm});
            skLineSegment(sketch, "E6.45.5", {"start": v(24.34, 25.37) * mm, "end": v(25.79, 24.82) * mm});
            skArc(sketch, "E6.45.6", {"start": v(23.15, 27.3) * mm, "mid": v(22.88, 27.65) * mm, "end": v(22.47, 27.85) * mm});
            skArc(sketch, "E6.45.7", {"start": v(26.16, 24.57) * mm, "mid": v(25.99, 24.71) * mm, "end": v(25.79, 24.82) * mm});
            skLineSegment(sketch, "E6.46.0", {"start": v(19.55, 29.98) * mm, "end": v(20.36, 28.67) * mm});
            skPoint(sketch, "E6.46.1", {"position": v(20.57, 28.32) * mm});
            skPoint(sketch, "E6.46.2", {"position": v(19.29, 30.4) * mm});
            skPoint(sketch, "E6.46.3", {"position": v(22.95, 27.74) * mm});
            skArc(sketch, "E6.46.4", {"start": v(20.36, 28.67) * mm, "mid": v(20.62, 28.38) * mm, "end": v(20.97, 28.22) * mm});
            skLineSegment(sketch, "E6.46.5", {"start": v(20.97, 28.22) * mm, "end": v(22.47, 27.85) * mm});
            skArc(sketch, "E6.46.6", {"start": v(19.55, 29.98) * mm, "mid": v(19.23, 30.3) * mm, "end": v(18.8, 30.45) * mm});
            skArc(sketch, "E6.46.7", {"start": v(22.88, 27.65) * mm, "mid": v(22.69, 27.78) * mm, "end": v(22.47, 27.85) * mm});
            skLineSegment(sketch, "E6.47.0", {"start": v(15.63, 32.2) * mm, "end": v(16.6, 31) * mm});
            skPoint(sketch, "E6.47.1", {"position": v(16.86, 30.67) * mm});
            skPoint(sketch, "E6.47.2", {"position": v(15.33, 32.57) * mm});
            skPoint(sketch, "E6.47.3", {"position": v(19.29, 30.4) * mm});
            skArc(sketch, "E6.47.4", {"start": v(16.6, 31) * mm, "mid": v(16.9, 30.74) * mm, "end": v(17.27, 30.62) * mm});
            skLineSegment(sketch, "E6.47.5", {"start": v(17.27, 30.62) * mm, "end": v(18.8, 30.45) * mm});
            skArc(sketch, "E6.47.6", {"start": v(15.63, 32.2) * mm, "mid": v(15.28, 32.47) * mm, "end": v(14.84, 32.57) * mm});
            skArc(sketch, "E6.47.7", {"start": v(19.23, 30.3) * mm, "mid": v(19.03, 30.4) * mm, "end": v(18.8, 30.45) * mm});
            skLineSegment(sketch, "E6.48.0", {"start": v(11.47, 33.9) * mm, "end": v(12.59, 32.83) * mm});
            skPoint(sketch, "E6.48.1", {"position": v(12.88, 32.54) * mm});
            skPoint(sketch, "E6.48.2", {"position": v(11.12, 34.24) * mm});
            skPoint(sketch, "E6.48.3", {"position": v(15.33, 32.57) * mm});
            skArc(sketch, "E6.48.4", {"start": v(12.59, 32.83) * mm, "mid": v(12.91, 32.62) * mm, "end": v(13.3, 32.55) * mm});
            skLineSegment(sketch, "E6.48.5", {"start": v(13.3, 32.55) * mm, "end": v(14.84, 32.57) * mm});
            skArc(sketch, "E6.48.6", {"start": v(11.47, 33.9) * mm, "mid": v(11.09, 34.13) * mm, "end": v(10.64, 34.17) * mm});
            skArc(sketch, "E6.48.7", {"start": v(15.28, 32.47) * mm, "mid": v(15.07, 32.54) * mm, "end": v(14.84, 32.57) * mm});
            skLineSegment(sketch, "E6.49.0", {"start": v(7.14, 35.07) * mm, "end": v(8.37, 34.15) * mm});
            skPoint(sketch, "E6.49.1", {"position": v(8.7, 33.9) * mm});
            skPoint(sketch, "E6.49.3", {"position": v(11.12, 34.24) * mm});
            skArc(sketch, "E6.49.4", {"start": v(8.37, 34.15) * mm, "mid": v(8.72, 33.98) * mm, "end": v(9.11, 33.96) * mm});
            skLineSegment(sketch, "E6.49.5", {"start": v(9.11, 33.96) * mm, "end": v(10.64, 34.17) * mm});
            skArc(sketch, "E6.49.6", {"start": v(7.14, 35.07) * mm, "mid": v(6.72, 35.25) * mm, "end": v(6.28, 35.24) * mm});
            skArc(sketch, "E6.49.7", {"start": v(11.09, 34.13) * mm, "mid": v(10.87, 34.18) * mm, "end": v(10.64, 34.17) * mm});
            skSolve(sketch);
        }
        {
            var Q0;
            Q0=makeQuery(id+"F0.imprint","IMPRINT",FACE,{"disambiguationData":[TD([[makeQuery(id+"F0.imprint","IMPRINT",EDGE,{"derivedFrom":sQuery(id+"F0.wireOp",EDGE,"E0")}),-1.0]])]});
            extrude(context, id + "F1", {"entities" : qUnion([Q0]), "depth" : 39.8 * mm});
        }
        {
            var Q0;
            Q0=makeQuery(id+"F1.opExtrude","CAP_FACE",FACE,{"disambiguationData":[OSD([sQuery(id+"F0.wireOp",EDGE,"E0"),sQuery(id+"F0.wireOp",EDGE,"E1"),sQuery(id+"F0.wireOp",EDGE,"E2"),sQuery(id+"F0.wireOp",EDGE,"E3.filletArc"),sQuery(id+"F0.wireOp",EDGE,"E4.filletArc"),sQuery(id+"F0.wireOp",EDGE,"E6.1.0"),sQuery(id+"F0.wireOp",EDGE,"E6.1.4"),sQuery(id+"F0.wireOp",EDGE,"E6.1.5"),sQuery(id+"F0.wireOp",EDGE,"E6.1.6"),sQuery(id+"F0.wireOp",EDGE,"E6.1.7"),sQuery(id+"F0.wireOp",EDGE,"E6.2.0"),sQuery(id+"F0.wireOp",EDGE,"E6.2.4"),sQuery(id+"F0.wireOp",EDGE,"E6.2.5"),sQuery(id+"F0.wireOp",EDGE,"E6.2.6"),sQuery(id+"F0.wireOp",EDGE,"E6.2.7"),sQuery(id+"F0.wireOp",EDGE,"E6.3.0"),sQuery(id+"F0.wireOp",EDGE,"E6.3.4"),sQuery(id+"F0.wireOp",EDGE,"E6.3.5"),sQuery(id+"F0.wireOp",EDGE,"E6.3.6"),sQuery(id+"F0.wireOp",EDGE,"E6.3.7"),sQuery(id+"F0.wireOp",EDGE,"E6.4.0"),sQuery(id+"F0.wireOp",EDGE,"E6.4.4"),sQuery(id+"F0.wireOp",EDGE,"E6.4.5"),sQuery(id+"F0.wireOp",EDGE,"E6.4.6"),sQuery(id+"F0.wireOp",EDGE,"E6.4.7"),sQuery(id+"F0.wireOp",EDGE,"E6.5.0"),sQuery(id+"F0.wireOp",EDGE,"E6.5.4"),sQuery(id+"F0.wireOp",EDGE,"E6.5.5"),sQuery(id+"F0.wireOp",EDGE,"E6.5.6"),sQuery(id+"F0.wireOp",EDGE,"E6.5.7"),sQuery(id+"F0.wireOp",EDGE,"E6.6.0"),sQuery(id+"F0.wireOp",EDGE,"E6.6.4"),sQuery(id+"F0.wireOp",EDGE,"E6.6.5"),sQuery(id+"F0.wireOp",EDGE,"E6.6.6"),sQuery(id+"F0.wireOp",EDGE,"E6.6.7"),sQuery(id+"F0.wireOp",EDGE,"E6.7.0"),sQuery(id+"F0.wireOp",EDGE,"E6.7.4"),sQuery(id+"F0.wireOp",EDGE,"E6.7.5"),sQuery(id+"F0.wireOp",EDGE,"E6.7.6"),sQuery(id+"F0.wireOp",EDGE,"E6.7.7"),sQuery(id+"F0.wireOp",EDGE,"E6.8.0"),sQuery(id+"F0.wireOp",EDGE,"E6.8.4"),sQuery(id+"F0.wireOp",EDGE,"E6.8.5"),sQuery(id+"F0.wireOp",EDGE,"E6.8.6"),sQuery(id+"F0.wireOp",EDGE,"E6.8.7"),sQuery(id+"F0.wireOp",EDGE,"E6.9.0"),sQuery(id+"F0.wireOp",EDGE,"E6.9.4"),sQuery(id+"F0.wireOp",EDGE,"E6.9.5"),sQuery(id+"F0.wireOp",EDGE,"E6.9.6"),sQuery(id+"F0.wireOp",EDGE,"E6.9.7"),sQuery(id+"F0.wireOp",EDGE,"E6.10.0"),sQuery(id+"F0.wireOp",EDGE,"E6.10.4"),sQuery(id+"F0.wireOp",EDGE,"E6.10.5"),sQuery(id+"F0.wireOp",EDGE,"E6.10.6"),sQuery(id+"F0.wireOp",EDGE,"E6.10.7"),sQuery(id+"F0.wireOp",EDGE,"E6.11.0"),sQuery(id+"F0.wireOp",EDGE,"E6.11.4"),sQuery(id+"F0.wireOp",EDGE,"E6.11.5"),sQuery(id+"F0.wireOp",EDGE,"E6.11.6"),sQuery(id+"F0.wireOp",EDGE,"E6.11.7"),sQuery(id+"F0.wireOp",EDGE,"E6.12.0"),sQuery(id+"F0.wireOp",EDGE,"E6.12.4"),sQuery(id+"F0.wireOp",EDGE,"E6.12.5"),sQuery(id+"F0.wireOp",EDGE,"E6.12.6"),sQuery(id+"F0.wireOp",EDGE,"E6.12.7"),sQuery(id+"F0.wireOp",EDGE,"E6.13.0"),sQuery(id+"F0.wireOp",EDGE,"E6.13.4"),sQuery(id+"F0.wireOp",EDGE,"E6.13.5"),sQuery(id+"F0.wireOp",EDGE,"E6.13.6"),sQuery(id+"F0.wireOp",EDGE,"E6.13.7"),sQuery(id+"F0.wireOp",EDGE,"E6.14.0"),sQuery(id+"F0.wireOp",EDGE,"E6.14.4"),sQuery(id+"F0.wireOp",EDGE,"E6.14.5"),sQuery(id+"F0.wireOp",EDGE,"E6.14.6"),sQuery(id+"F0.wireOp",EDGE,"E6.14.7"),sQuery(id+"F0.wireOp",EDGE,"E6.15.0"),sQuery(id+"F0.wireOp",EDGE,"E6.15.4"),sQuery(id+"F0.wireOp",EDGE,"E6.15.5"),sQuery(id+"F0.wireOp",EDGE,"E6.15.6"),sQuery(id+"F0.wireOp",EDGE,"E6.15.7"),sQuery(id+"F0.wireOp",EDGE,"E6.16.0"),sQuery(id+"F0.wireOp",EDGE,"E6.16.4"),sQuery(id+"F0.wireOp",EDGE,"E6.16.5"),sQuery(id+"F0.wireOp",EDGE,"E6.16.6"),sQuery(id+"F0.wireOp",EDGE,"E6.16.7"),sQuery(id+"F0.wireOp",EDGE,"E6.17.0"),sQuery(id+"F0.wireOp",EDGE,"E6.17.4"),sQuery(id+"F0.wireOp",EDGE,"E6.17.5"),sQuery(id+"F0.wireOp",EDGE,"E6.17.6"),sQuery(id+"F0.wireOp",EDGE,"E6.17.7"),sQuery(id+"F0.wireOp",EDGE,"E6.18.0"),sQuery(id+"F0.wireOp",EDGE,"E6.18.4"),sQuery(id+"F0.wireOp",EDGE,"E6.18.5"),sQuery(id+"F0.wireOp",EDGE,"E6.18.6"),sQuery(id+"F0.wireOp",EDGE,"E6.18.7"),sQuery(id+"F0.wireOp",EDGE,"E6.19.0"),sQuery(id+"F0.wireOp",EDGE,"E6.19.4"),sQuery(id+"F0.wireOp",EDGE,"E6.19.5"),sQuery(id+"F0.wireOp",EDGE,"E6.19.6"),sQuery(id+"F0.wireOp",EDGE,"E6.19.7"),sQuery(id+"F0.wireOp",EDGE,"E6.20.0"),sQuery(id+"F0.wireOp",EDGE,"E6.20.4"),sQuery(id+"F0.wireOp",EDGE,"E6.20.5"),sQuery(id+"F0.wireOp",EDGE,"E6.20.6"),sQuery(id+"F0.wireOp",EDGE,"E6.20.7"),sQuery(id+"F0.wireOp",EDGE,"E6.21.0"),sQuery(id+"F0.wireOp",EDGE,"E6.21.4"),sQuery(id+"F0.wireOp",EDGE,"E6.21.5"),sQuery(id+"F0.wireOp",EDGE,"E6.21.6"),sQuery(id+"F0.wireOp",EDGE,"E6.21.7"),sQuery(id+"F0.wireOp",EDGE,"E6.22.0"),sQuery(id+"F0.wireOp",EDGE,"E6.22.4"),sQuery(id+"F0.wireOp",EDGE,"E6.22.5"),sQuery(id+"F0.wireOp",EDGE,"E6.22.6"),sQuery(id+"F0.wireOp",EDGE,"E6.22.7"),sQuery(id+"F0.wireOp",EDGE,"E6.23.0"),sQuery(id+"F0.wireOp",EDGE,"E6.23.4"),sQuery(id+"F0.wireOp",EDGE,"E6.23.5"),sQuery(id+"F0.wireOp",EDGE,"E6.23.6"),sQuery(id+"F0.wireOp",EDGE,"E6.23.7"),sQuery(id+"F0.wireOp",EDGE,"E6.24.0"),sQuery(id+"F0.wireOp",EDGE,"E6.24.4"),sQuery(id+"F0.wireOp",EDGE,"E6.24.5"),sQuery(id+"F0.wireOp",EDGE,"E6.24.6"),sQuery(id+"F0.wireOp",EDGE,"E6.24.7"),sQuery(id+"F0.wireOp",EDGE,"E6.25.0"),sQuery(id+"F0.wireOp",EDGE,"E6.25.4"),sQuery(id+"F0.wireOp",EDGE,"E6.25.5"),sQuery(id+"F0.wireOp",EDGE,"E6.25.6"),sQuery(id+"F0.wireOp",EDGE,"E6.25.7"),sQuery(id+"F0.wireOp",EDGE,"E6.26.0"),sQuery(id+"F0.wireOp",EDGE,"E6.26.4"),sQuery(id+"F0.wireOp",EDGE,"E6.26.5"),sQuery(id+"F0.wireOp",EDGE,"E6.26.6"),sQuery(id+"F0.wireOp",EDGE,"E6.26.7"),sQuery(id+"F0.wireOp",EDGE,"E6.27.0"),sQuery(id+"F0.wireOp",EDGE,"E6.27.4"),sQuery(id+"F0.wireOp",EDGE,"E6.27.5"),sQuery(id+"F0.wireOp",EDGE,"E6.27.6"),sQuery(id+"F0.wireOp",EDGE,"E6.27.7"),sQuery(id+"F0.wireOp",EDGE,"E6.28.0"),sQuery(id+"F0.wireOp",EDGE,"E6.28.4"),sQuery(id+"F0.wireOp",EDGE,"E6.28.5"),sQuery(id+"F0.wireOp",EDGE,"E6.28.6"),sQuery(id+"F0.wireOp",EDGE,"E6.28.7"),sQuery(id+"F0.wireOp",EDGE,"E6.29.0"),sQuery(id+"F0.wireOp",EDGE,"E6.29.4"),sQuery(id+"F0.wireOp",EDGE,"E6.29.5"),sQuery(id+"F0.wireOp",EDGE,"E6.29.6"),sQuery(id+"F0.wireOp",EDGE,"E6.29.7"),sQuery(id+"F0.wireOp",EDGE,"E6.30.0"),sQuery(id+"F0.wireOp",EDGE,"E6.30.4"),sQuery(id+"F0.wireOp",EDGE,"E6.30.5"),sQuery(id+"F0.wireOp",EDGE,"E6.30.6"),sQuery(id+"F0.wireOp",EDGE,"E6.30.7"),sQuery(id+"F0.wireOp",EDGE,"E6.31.0"),sQuery(id+"F0.wireOp",EDGE,"E6.31.4"),sQuery(id+"F0.wireOp",EDGE,"E6.31.5"),sQuery(id+"F0.wireOp",EDGE,"E6.31.6"),sQuery(id+"F0.wireOp",EDGE,"E6.31.7"),sQuery(id+"F0.wireOp",EDGE,"E6.32.0"),sQuery(id+"F0.wireOp",EDGE,"E6.32.4"),sQuery(id+"F0.wireOp",EDGE,"E6.32.5"),sQuery(id+"F0.wireOp",EDGE,"E6.32.6"),sQuery(id+"F0.wireOp",EDGE,"E6.32.7"),sQuery(id+"F0.wireOp",EDGE,"E6.33.0"),sQuery(id+"F0.wireOp",EDGE,"E6.33.4"),sQuery(id+"F0.wireOp",EDGE,"E6.33.5"),sQuery(id+"F0.wireOp",EDGE,"E6.33.6"),sQuery(id+"F0.wireOp",EDGE,"E6.33.7"),sQuery(id+"F0.wireOp",EDGE,"E6.34.0"),sQuery(id+"F0.wireOp",EDGE,"E6.34.4"),sQuery(id+"F0.wireOp",EDGE,"E6.34.5"),sQuery(id+"F0.wireOp",EDGE,"E6.34.6"),sQuery(id+"F0.wireOp",EDGE,"E6.34.7"),sQuery(id+"F0.wireOp",EDGE,"E6.35.0"),sQuery(id+"F0.wireOp",EDGE,"E6.35.4"),sQuery(id+"F0.wireOp",EDGE,"E6.35.5"),sQuery(id+"F0.wireOp",EDGE,"E6.35.6"),sQuery(id+"F0.wireOp",EDGE,"E6.35.7"),sQuery(id+"F0.wireOp",EDGE,"E6.36.0"),sQuery(id+"F0.wireOp",EDGE,"E6.36.4"),sQuery(id+"F0.wireOp",EDGE,"E6.36.5"),sQuery(id+"F0.wireOp",EDGE,"E6.36.6"),sQuery(id+"F0.wireOp",EDGE,"E6.36.7"),sQuery(id+"F0.wireOp",EDGE,"E6.37.0"),sQuery(id+"F0.wireOp",EDGE,"E6.37.4"),sQuery(id+"F0.wireOp",EDGE,"E6.37.5"),sQuery(id+"F0.wireOp",EDGE,"E6.37.6"),sQuery(id+"F0.wireOp",EDGE,"E6.37.7"),sQuery(id+"F0.wireOp",EDGE,"E6.38.0"),sQuery(id+"F0.wireOp",EDGE,"E6.38.4"),sQuery(id+"F0.wireOp",EDGE,"E6.38.5"),sQuery(id+"F0.wireOp",EDGE,"E6.38.6"),sQuery(id+"F0.wireOp",EDGE,"E6.38.7"),sQuery(id+"F0.wireOp",EDGE,"E6.39.0"),sQuery(id+"F0.wireOp",EDGE,"E6.39.4"),sQuery(id+"F0.wireOp",EDGE,"E6.39.5"),sQuery(id+"F0.wireOp",EDGE,"E6.39.6"),sQuery(id+"F0.wireOp",EDGE,"E6.39.7"),sQuery(id+"F0.wireOp",EDGE,"E6.40.0"),sQuery(id+"F0.wireOp",EDGE,"E6.40.4"),sQuery(id+"F0.wireOp",EDGE,"E6.40.5"),sQuery(id+"F0.wireOp",EDGE,"E6.40.6"),sQuery(id+"F0.wireOp",EDGE,"E6.40.7"),sQuery(id+"F0.wireOp",EDGE,"E6.41.0"),sQuery(id+"F0.wireOp",EDGE,"E6.41.4"),sQuery(id+"F0.wireOp",EDGE,"E6.41.5"),sQuery(id+"F0.wireOp",EDGE,"E6.41.6"),sQuery(id+"F0.wireOp",EDGE,"E6.41.7"),sQuery(id+"F0.wireOp",EDGE,"E6.42.0"),sQuery(id+"F0.wireOp",EDGE,"E6.42.4"),sQuery(id+"F0.wireOp",EDGE,"E6.42.5"),sQuery(id+"F0.wireOp",EDGE,"E6.42.6"),sQuery(id+"F0.wireOp",EDGE,"E6.42.7"),sQuery(id+"F0.wireOp",EDGE,"E6.43.0"),sQuery(id+"F0.wireOp",EDGE,"E6.43.4"),sQuery(id+"F0.wireOp",EDGE,"E6.43.5"),sQuery(id+"F0.wireOp",EDGE,"E6.43.6"),sQuery(id+"F0.wireOp",EDGE,"E6.43.7"),sQuery(id+"F0.wireOp",EDGE,"E6.44.0"),sQuery(id+"F0.wireOp",EDGE,"E6.44.4"),sQuery(id+"F0.wireOp",EDGE,"E6.44.5"),sQuery(id+"F0.wireOp",EDGE,"E6.44.6"),sQuery(id+"F0.wireOp",EDGE,"E6.44.7"),sQuery(id+"F0.wireOp",EDGE,"E6.45.0"),sQuery(id+"F0.wireOp",EDGE,"E6.45.4"),sQuery(id+"F0.wireOp",EDGE,"E6.45.5"),sQuery(id+"F0.wireOp",EDGE,"E6.45.6"),sQuery(id+"F0.wireOp",EDGE,"E6.45.7"),sQuery(id+"F0.wireOp",EDGE,"E6.46.0"),sQuery(id+"F0.wireOp",EDGE,"E6.46.4"),sQuery(id+"F0.wireOp",EDGE,"E6.46.5"),sQuery(id+"F0.wireOp",EDGE,"E6.46.6"),sQuery(id+"F0.wireOp",EDGE,"E6.46.7"),sQuery(id+"F0.wireOp",EDGE,"E6.47.0"),sQuery(id+"F0.wireOp",EDGE,"E6.47.4"),sQuery(id+"F0.wireOp",EDGE,"E6.47.5"),sQuery(id+"F0.wireOp",EDGE,"E6.47.6"),sQuery(id+"F0.wireOp",EDGE,"E6.47.7"),sQuery(id+"F0.wireOp",EDGE,"E6.48.0"),sQuery(id+"F0.wireOp",EDGE,"E6.48.4"),sQuery(id+"F0.wireOp",EDGE,"E6.48.5"),sQuery(id+"F0.wireOp",EDGE,"E6.48.6"),sQuery(id+"F0.wireOp",EDGE,"E6.48.7"),sQuery(id+"F0.wireOp",EDGE,"E6.49.0"),sQuery(id+"F0.wireOp",EDGE,"E6.49.4"),sQuery(id+"F0.wireOp",EDGE,"E6.49.5"),sQuery(id+"F0.wireOp",EDGE,"E6.49.6"),sQuery(id+"F0.wireOp",EDGE,"E6.49.7")])],"isStart":false});
            var sketch = newSketch(context, id + "F2", { "sketchPlane" : qUnion([Q0])});
            skCircle(sketch, "E7.0", {"center": v(0, 0) * mm, "radius": 34.35 * mm});
            skSolve(sketch);
        }
        {
            var Q0;
            Q0 = qSketchRegion(id + "F2", true);
            extrude(context, id + "F3", {"entities" : qUnion([Q0]), "operationType" : NewBodyOperationType.REMOVE, "oppositeDirection" : true, "depth" : 6.5 * mm});
        }
        {
            var Q0;
            Q0=qCreatedBy(makeId("Right.planeOp"),FACE);
            var sketch = newSketch(context, id + "F4", { "sketchPlane" : qUnion([Q0])});
            skLineSegment(sketch, "E8.0.0", {"start": v(-34.35, 33.3) * mm, "end": v(34.35, 33.3) * mm});
            skLineSegment(sketch, "E9", {"start": v(-33.05, 0.2) * mm, "end": v(-33.05, 33.3) * mm});
            skLineSegment(sketch, "E10", {"start": v(33.05, 33.3) * mm, "end": v(33.05, 0.2) * mm});
            skLineSegment(sketch, "E11", {"start": v(34.35, 33.3) * mm, "end": v(33.05, 27.46) * mm});
            skLineSegment(sketch, "E12", {"start": v(34.35, 33.3) * mm, "end": v(33.05, 33.3) * mm});
            skLineSegment(sketch, "E13", {"start": v(33.05, 27.46) * mm, "end": v(33.05, 33.3) * mm});
            skLineSegment(sketch, "E14", {"start": v(0, 0) * mm, "end": v(0, 57.54) * mm});
            skSolve(sketch);
        }
        {
            var Q0;
            Q0=makeQuery(id+"F4.imprint","IMPRINT",FACE,{"disambiguationData":[TD([[makeQuery(id+"F4.imprint","IMPRINT",EDGE,{"derivedFrom":sQuery(id+"F4.wireOp",EDGE,"E11")}),-1.0]])]});
            var Q1;
            Q1=sQuery(id+"F4.wireOp",EDGE,"E14");
            revolve(context, id + "F5", {"operationType" : NewBodyOperationType.REMOVE, "entities" : qUnion([Q0]), "axis" : qUnion([Q1]), "revolveType" : RevolveType.FULL, "oppositeDirection" : true});
        }
        {
            var Q0;
            Q0=makeQuery(id+"F1.opExtrude","CAP_FACE",FACE,{"disambiguationData":[OSD([sQuery(id+"F0.wireOp",EDGE,"E0"),sQuery(id+"F0.wireOp",EDGE,"E1"),sQuery(id+"F0.wireOp",EDGE,"E2"),sQuery(id+"F0.wireOp",EDGE,"E3.filletArc"),sQuery(id+"F0.wireOp",EDGE,"E4.filletArc"),sQuery(id+"F0.wireOp",EDGE,"E6.1.0"),sQuery(id+"F0.wireOp",EDGE,"E6.1.4"),sQuery(id+"F0.wireOp",EDGE,"E6.1.5"),sQuery(id+"F0.wireOp",EDGE,"E6.1.6"),sQuery(id+"F0.wireOp",EDGE,"E6.1.7"),sQuery(id+"F0.wireOp",EDGE,"E6.2.0"),sQuery(id+"F0.wireOp",EDGE,"E6.2.4"),sQuery(id+"F0.wireOp",EDGE,"E6.2.5"),sQuery(id+"F0.wireOp",EDGE,"E6.2.6"),sQuery(id+"F0.wireOp",EDGE,"E6.2.7"),sQuery(id+"F0.wireOp",EDGE,"E6.3.0"),sQuery(id+"F0.wireOp",EDGE,"E6.3.4"),sQuery(id+"F0.wireOp",EDGE,"E6.3.5"),sQuery(id+"F0.wireOp",EDGE,"E6.3.6"),sQuery(id+"F0.wireOp",EDGE,"E6.3.7"),sQuery(id+"F0.wireOp",EDGE,"E6.4.0"),sQuery(id+"F0.wireOp",EDGE,"E6.4.4"),sQuery(id+"F0.wireOp",EDGE,"E6.4.5"),sQuery(id+"F0.wireOp",EDGE,"E6.4.6"),sQuery(id+"F0.wireOp",EDGE,"E6.4.7"),sQuery(id+"F0.wireOp",EDGE,"E6.5.0"),sQuery(id+"F0.wireOp",EDGE,"E6.5.4"),sQuery(id+"F0.wireOp",EDGE,"E6.5.5"),sQuery(id+"F0.wireOp",EDGE,"E6.5.6"),sQuery(id+"F0.wireOp",EDGE,"E6.5.7"),sQuery(id+"F0.wireOp",EDGE,"E6.6.0"),sQuery(id+"F0.wireOp",EDGE,"E6.6.4"),sQuery(id+"F0.wireOp",EDGE,"E6.6.5"),sQuery(id+"F0.wireOp",EDGE,"E6.6.6"),sQuery(id+"F0.wireOp",EDGE,"E6.6.7"),sQuery(id+"F0.wireOp",EDGE,"E6.7.0"),sQuery(id+"F0.wireOp",EDGE,"E6.7.4"),sQuery(id+"F0.wireOp",EDGE,"E6.7.5"),sQuery(id+"F0.wireOp",EDGE,"E6.7.6"),sQuery(id+"F0.wireOp",EDGE,"E6.7.7"),sQuery(id+"F0.wireOp",EDGE,"E6.8.0"),sQuery(id+"F0.wireOp",EDGE,"E6.8.4"),sQuery(id+"F0.wireOp",EDGE,"E6.8.5"),sQuery(id+"F0.wireOp",EDGE,"E6.8.6"),sQuery(id+"F0.wireOp",EDGE,"E6.8.7"),sQuery(id+"F0.wireOp",EDGE,"E6.9.0"),sQuery(id+"F0.wireOp",EDGE,"E6.9.4"),sQuery(id+"F0.wireOp",EDGE,"E6.9.5"),sQuery(id+"F0.wireOp",EDGE,"E6.9.6"),sQuery(id+"F0.wireOp",EDGE,"E6.9.7"),sQuery(id+"F0.wireOp",EDGE,"E6.10.0"),sQuery(id+"F0.wireOp",EDGE,"E6.10.4"),sQuery(id+"F0.wireOp",EDGE,"E6.10.5"),sQuery(id+"F0.wireOp",EDGE,"E6.10.6"),sQuery(id+"F0.wireOp",EDGE,"E6.10.7"),sQuery(id+"F0.wireOp",EDGE,"E6.11.0"),sQuery(id+"F0.wireOp",EDGE,"E6.11.4"),sQuery(id+"F0.wireOp",EDGE,"E6.11.5"),sQuery(id+"F0.wireOp",EDGE,"E6.11.6"),sQuery(id+"F0.wireOp",EDGE,"E6.11.7"),sQuery(id+"F0.wireOp",EDGE,"E6.12.0"),sQuery(id+"F0.wireOp",EDGE,"E6.12.4"),sQuery(id+"F0.wireOp",EDGE,"E6.12.5"),sQuery(id+"F0.wireOp",EDGE,"E6.12.6"),sQuery(id+"F0.wireOp",EDGE,"E6.12.7"),sQuery(id+"F0.wireOp",EDGE,"E6.13.0"),sQuery(id+"F0.wireOp",EDGE,"E6.13.4"),sQuery(id+"F0.wireOp",EDGE,"E6.13.5"),sQuery(id+"F0.wireOp",EDGE,"E6.13.6"),sQuery(id+"F0.wireOp",EDGE,"E6.13.7"),sQuery(id+"F0.wireOp",EDGE,"E6.14.0"),sQuery(id+"F0.wireOp",EDGE,"E6.14.4"),sQuery(id+"F0.wireOp",EDGE,"E6.14.5"),sQuery(id+"F0.wireOp",EDGE,"E6.14.6"),sQuery(id+"F0.wireOp",EDGE,"E6.14.7"),sQuery(id+"F0.wireOp",EDGE,"E6.15.0"),sQuery(id+"F0.wireOp",EDGE,"E6.15.4"),sQuery(id+"F0.wireOp",EDGE,"E6.15.5"),sQuery(id+"F0.wireOp",EDGE,"E6.15.6"),sQuery(id+"F0.wireOp",EDGE,"E6.15.7"),sQuery(id+"F0.wireOp",EDGE,"E6.16.0"),sQuery(id+"F0.wireOp",EDGE,"E6.16.4"),sQuery(id+"F0.wireOp",EDGE,"E6.16.5"),sQuery(id+"F0.wireOp",EDGE,"E6.16.6"),sQuery(id+"F0.wireOp",EDGE,"E6.16.7"),sQuery(id+"F0.wireOp",EDGE,"E6.17.0"),sQuery(id+"F0.wireOp",EDGE,"E6.17.4"),sQuery(id+"F0.wireOp",EDGE,"E6.17.5"),sQuery(id+"F0.wireOp",EDGE,"E6.17.6"),sQuery(id+"F0.wireOp",EDGE,"E6.17.7"),sQuery(id+"F0.wireOp",EDGE,"E6.18.0"),sQuery(id+"F0.wireOp",EDGE,"E6.18.4"),sQuery(id+"F0.wireOp",EDGE,"E6.18.5"),sQuery(id+"F0.wireOp",EDGE,"E6.18.6"),sQuery(id+"F0.wireOp",EDGE,"E6.18.7"),sQuery(id+"F0.wireOp",EDGE,"E6.19.0"),sQuery(id+"F0.wireOp",EDGE,"E6.19.4"),sQuery(id+"F0.wireOp",EDGE,"E6.19.5"),sQuery(id+"F0.wireOp",EDGE,"E6.19.6"),sQuery(id+"F0.wireOp",EDGE,"E6.19.7"),sQuery(id+"F0.wireOp",EDGE,"E6.20.0"),sQuery(id+"F0.wireOp",EDGE,"E6.20.4"),sQuery(id+"F0.wireOp",EDGE,"E6.20.5"),sQuery(id+"F0.wireOp",EDGE,"E6.20.6"),sQuery(id+"F0.wireOp",EDGE,"E6.20.7"),sQuery(id+"F0.wireOp",EDGE,"E6.21.0"),sQuery(id+"F0.wireOp",EDGE,"E6.21.4"),sQuery(id+"F0.wireOp",EDGE,"E6.21.5"),sQuery(id+"F0.wireOp",EDGE,"E6.21.6"),sQuery(id+"F0.wireOp",EDGE,"E6.21.7"),sQuery(id+"F0.wireOp",EDGE,"E6.22.0"),sQuery(id+"F0.wireOp",EDGE,"E6.22.4"),sQuery(id+"F0.wireOp",EDGE,"E6.22.5"),sQuery(id+"F0.wireOp",EDGE,"E6.22.6"),sQuery(id+"F0.wireOp",EDGE,"E6.22.7"),sQuery(id+"F0.wireOp",EDGE,"E6.23.0"),sQuery(id+"F0.wireOp",EDGE,"E6.23.4"),sQuery(id+"F0.wireOp",EDGE,"E6.23.5"),sQuery(id+"F0.wireOp",EDGE,"E6.23.6"),sQuery(id+"F0.wireOp",EDGE,"E6.23.7"),sQuery(id+"F0.wireOp",EDGE,"E6.24.0"),sQuery(id+"F0.wireOp",EDGE,"E6.24.4"),sQuery(id+"F0.wireOp",EDGE,"E6.24.5"),sQuery(id+"F0.wireOp",EDGE,"E6.24.6"),sQuery(id+"F0.wireOp",EDGE,"E6.24.7"),sQuery(id+"F0.wireOp",EDGE,"E6.25.0"),sQuery(id+"F0.wireOp",EDGE,"E6.25.4"),sQuery(id+"F0.wireOp",EDGE,"E6.25.5"),sQuery(id+"F0.wireOp",EDGE,"E6.25.6"),sQuery(id+"F0.wireOp",EDGE,"E6.25.7"),sQuery(id+"F0.wireOp",EDGE,"E6.26.0"),sQuery(id+"F0.wireOp",EDGE,"E6.26.4"),sQuery(id+"F0.wireOp",EDGE,"E6.26.5"),sQuery(id+"F0.wireOp",EDGE,"E6.26.6"),sQuery(id+"F0.wireOp",EDGE,"E6.26.7"),sQuery(id+"F0.wireOp",EDGE,"E6.27.0"),sQuery(id+"F0.wireOp",EDGE,"E6.27.4"),sQuery(id+"F0.wireOp",EDGE,"E6.27.5"),sQuery(id+"F0.wireOp",EDGE,"E6.27.6"),sQuery(id+"F0.wireOp",EDGE,"E6.27.7"),sQuery(id+"F0.wireOp",EDGE,"E6.28.0"),sQuery(id+"F0.wireOp",EDGE,"E6.28.4"),sQuery(id+"F0.wireOp",EDGE,"E6.28.5"),sQuery(id+"F0.wireOp",EDGE,"E6.28.6"),sQuery(id+"F0.wireOp",EDGE,"E6.28.7"),sQuery(id+"F0.wireOp",EDGE,"E6.29.0"),sQuery(id+"F0.wireOp",EDGE,"E6.29.4"),sQuery(id+"F0.wireOp",EDGE,"E6.29.5"),sQuery(id+"F0.wireOp",EDGE,"E6.29.6"),sQuery(id+"F0.wireOp",EDGE,"E6.29.7"),sQuery(id+"F0.wireOp",EDGE,"E6.30.0"),sQuery(id+"F0.wireOp",EDGE,"E6.30.4"),sQuery(id+"F0.wireOp",EDGE,"E6.30.5"),sQuery(id+"F0.wireOp",EDGE,"E6.30.6"),sQuery(id+"F0.wireOp",EDGE,"E6.30.7"),sQuery(id+"F0.wireOp",EDGE,"E6.31.0"),sQuery(id+"F0.wireOp",EDGE,"E6.31.4"),sQuery(id+"F0.wireOp",EDGE,"E6.31.5"),sQuery(id+"F0.wireOp",EDGE,"E6.31.6"),sQuery(id+"F0.wireOp",EDGE,"E6.31.7"),sQuery(id+"F0.wireOp",EDGE,"E6.32.0"),sQuery(id+"F0.wireOp",EDGE,"E6.32.4"),sQuery(id+"F0.wireOp",EDGE,"E6.32.5"),sQuery(id+"F0.wireOp",EDGE,"E6.32.6"),sQuery(id+"F0.wireOp",EDGE,"E6.32.7"),sQuery(id+"F0.wireOp",EDGE,"E6.33.0"),sQuery(id+"F0.wireOp",EDGE,"E6.33.4"),sQuery(id+"F0.wireOp",EDGE,"E6.33.5"),sQuery(id+"F0.wireOp",EDGE,"E6.33.6"),sQuery(id+"F0.wireOp",EDGE,"E6.33.7"),sQuery(id+"F0.wireOp",EDGE,"E6.34.0"),sQuery(id+"F0.wireOp",EDGE,"E6.34.4"),sQuery(id+"F0.wireOp",EDGE,"E6.34.5"),sQuery(id+"F0.wireOp",EDGE,"E6.34.6"),sQuery(id+"F0.wireOp",EDGE,"E6.34.7"),sQuery(id+"F0.wireOp",EDGE,"E6.35.0"),sQuery(id+"F0.wireOp",EDGE,"E6.35.4"),sQuery(id+"F0.wireOp",EDGE,"E6.35.5"),sQuery(id+"F0.wireOp",EDGE,"E6.35.6"),sQuery(id+"F0.wireOp",EDGE,"E6.35.7"),sQuery(id+"F0.wireOp",EDGE,"E6.36.0"),sQuery(id+"F0.wireOp",EDGE,"E6.36.4"),sQuery(id+"F0.wireOp",EDGE,"E6.36.5"),sQuery(id+"F0.wireOp",EDGE,"E6.36.6"),sQuery(id+"F0.wireOp",EDGE,"E6.36.7"),sQuery(id+"F0.wireOp",EDGE,"E6.37.0"),sQuery(id+"F0.wireOp",EDGE,"E6.37.4"),sQuery(id+"F0.wireOp",EDGE,"E6.37.5"),sQuery(id+"F0.wireOp",EDGE,"E6.37.6"),sQuery(id+"F0.wireOp",EDGE,"E6.37.7"),sQuery(id+"F0.wireOp",EDGE,"E6.38.0"),sQuery(id+"F0.wireOp",EDGE,"E6.38.4"),sQuery(id+"F0.wireOp",EDGE,"E6.38.5"),sQuery(id+"F0.wireOp",EDGE,"E6.38.6"),sQuery(id+"F0.wireOp",EDGE,"E6.38.7"),sQuery(id+"F0.wireOp",EDGE,"E6.39.0"),sQuery(id+"F0.wireOp",EDGE,"E6.39.4"),sQuery(id+"F0.wireOp",EDGE,"E6.39.5"),sQuery(id+"F0.wireOp",EDGE,"E6.39.6"),sQuery(id+"F0.wireOp",EDGE,"E6.39.7"),sQuery(id+"F0.wireOp",EDGE,"E6.40.0"),sQuery(id+"F0.wireOp",EDGE,"E6.40.4"),sQuery(id+"F0.wireOp",EDGE,"E6.40.5"),sQuery(id+"F0.wireOp",EDGE,"E6.40.6"),sQuery(id+"F0.wireOp",EDGE,"E6.40.7"),sQuery(id+"F0.wireOp",EDGE,"E6.41.0"),sQuery(id+"F0.wireOp",EDGE,"E6.41.4"),sQuery(id+"F0.wireOp",EDGE,"E6.41.5"),sQuery(id+"F0.wireOp",EDGE,"E6.41.6"),sQuery(id+"F0.wireOp",EDGE,"E6.41.7"),sQuery(id+"F0.wireOp",EDGE,"E6.42.0"),sQuery(id+"F0.wireOp",EDGE,"E6.42.4"),sQuery(id+"F0.wireOp",EDGE,"E6.42.5"),sQuery(id+"F0.wireOp",EDGE,"E6.42.6"),sQuery(id+"F0.wireOp",EDGE,"E6.42.7"),sQuery(id+"F0.wireOp",EDGE,"E6.43.0"),sQuery(id+"F0.wireOp",EDGE,"E6.43.4"),sQuery(id+"F0.wireOp",EDGE,"E6.43.5"),sQuery(id+"F0.wireOp",EDGE,"E6.43.6"),sQuery(id+"F0.wireOp",EDGE,"E6.43.7"),sQuery(id+"F0.wireOp",EDGE,"E6.44.0"),sQuery(id+"F0.wireOp",EDGE,"E6.44.4"),sQuery(id+"F0.wireOp",EDGE,"E6.44.5"),sQuery(id+"F0.wireOp",EDGE,"E6.44.6"),sQuery(id+"F0.wireOp",EDGE,"E6.44.7"),sQuery(id+"F0.wireOp",EDGE,"E6.45.0"),sQuery(id+"F0.wireOp",EDGE,"E6.45.4"),sQuery(id+"F0.wireOp",EDGE,"E6.45.5"),sQuery(id+"F0.wireOp",EDGE,"E6.45.6"),sQuery(id+"F0.wireOp",EDGE,"E6.45.7"),sQuery(id+"F0.wireOp",EDGE,"E6.46.0"),sQuery(id+"F0.wireOp",EDGE,"E6.46.4"),sQuery(id+"F0.wireOp",EDGE,"E6.46.5"),sQuery(id+"F0.wireOp",EDGE,"E6.46.6"),sQuery(id+"F0.wireOp",EDGE,"E6.46.7"),sQuery(id+"F0.wireOp",EDGE,"E6.47.0"),sQuery(id+"F0.wireOp",EDGE,"E6.47.4"),sQuery(id+"F0.wireOp",EDGE,"E6.47.5"),sQuery(id+"F0.wireOp",EDGE,"E6.47.6"),sQuery(id+"F0.wireOp",EDGE,"E6.47.7"),sQuery(id+"F0.wireOp",EDGE,"E6.48.0"),sQuery(id+"F0.wireOp",EDGE,"E6.48.4"),sQuery(id+"F0.wireOp",EDGE,"E6.48.5"),sQuery(id+"F0.wireOp",EDGE,"E6.48.6"),sQuery(id+"F0.wireOp",EDGE,"E6.48.7"),sQuery(id+"F0.wireOp",EDGE,"E6.49.0"),sQuery(id+"F0.wireOp",EDGE,"E6.49.4"),sQuery(id+"F0.wireOp",EDGE,"E6.49.5"),sQuery(id+"F0.wireOp",EDGE,"E6.49.6"),sQuery(id+"F0.wireOp",EDGE,"E6.49.7")])],"isStart":false});
            var sketch = newSketch(context, id + "F6", { "sketchPlane" : qUnion([Q0])});
            skLineSegment(sketch, "E15", {"start": v(-34.35, 0) * mm, "end": v(34.35, 0) * mm});
            skCircle(sketch, "E16", {"center": v(0, 0) * mm, "radius": 34.5 * mm});
            skCircle(sketch, "E17", {"center": v(0, 0) * mm, "radius": 33.05 * mm});
            skSolve(sketch);
        }
        {
            var Q0;
            {var subQ0=sQuery(id+"F6.wireOp",EDGE,"E15");var subQ1=makeQuery(id+"F3.boolean.opBoolean","COPY",EDGE,{"derivedFrom":makeQuery(id+"F3.opExtrude","CAP_EDGE",EDGE,{"disambiguationData":[OSD([sQuery(id+"F2.wireOp",EDGE,"E7.0")])],"isStart":true})});var subQ2=makeQuery(id+"F6.imprint","INTERSECT",VERTEX,{"disambiguationData":[OD(0.0)],"derivedFrom":[subQ1,subQ0]});Q0=makeQuery(id+"F6.imprint","IMPRINT",FACE,{"disambiguationData":[TD([[makeQuery(id+"F6.imprint","IMPRINT",EDGE,{"disambiguationData":[TD([[subQ2,-1.0]])],"derivedFrom":subQ0}),-1.0]])]});}
            var Q1;
            {var subQ0=sQuery(id+"F6.wireOp",EDGE,"E15");var subQ1=makeQuery(id+"F3.boolean.opBoolean","COPY",EDGE,{"derivedFrom":makeQuery(id+"F3.opExtrude","CAP_EDGE",EDGE,{"disambiguationData":[OSD([sQuery(id+"F2.wireOp",EDGE,"E7.0")])],"isStart":true})});var subQ2=makeQuery(id+"F6.imprint","INTERSECT",VERTEX,{"disambiguationData":[OD(0.0)],"derivedFrom":[subQ1,subQ0]});Q1=makeQuery(id+"F6.imprint","IMPRINT",FACE,{"disambiguationData":[TD([[makeQuery(id+"F6.imprint","IMPRINT",EDGE,{"disambiguationData":[TD([[subQ2,-1.0]])],"derivedFrom":subQ0}),1.0]])]});}
            var Q2;
            Q2=makeQuery(id+"F6.imprint","IMPRINT",FACE,{"disambiguationData":[TD([[makeQuery(id+"F6.imprint","IMPRINT",EDGE,{"derivedFrom":sQuery(id+"F6.wireOp",EDGE,"E16")}),1.0]])]});
            extrude(context, id + "F7", {"entities" : qUnion([Q0, Q1, Q2]), "operationType" : NewBodyOperationType.ADD, "oppositeDirection" : true, "depth" : 2.8 * mm});
        }
        {
            var Q0;
            Q0=makeQuery(id+"F1.opExtrude","CAP_FACE",FACE,{"disambiguationData":[OSD([sQuery(id+"F0.wireOp",EDGE,"E0"),sQuery(id+"F0.wireOp",EDGE,"E1"),sQuery(id+"F0.wireOp",EDGE,"E2"),sQuery(id+"F0.wireOp",EDGE,"E3.filletArc"),sQuery(id+"F0.wireOp",EDGE,"E4.filletArc"),sQuery(id+"F0.wireOp",EDGE,"E6.1.0"),sQuery(id+"F0.wireOp",EDGE,"E6.1.4"),sQuery(id+"F0.wireOp",EDGE,"E6.1.5"),sQuery(id+"F0.wireOp",EDGE,"E6.1.6"),sQuery(id+"F0.wireOp",EDGE,"E6.1.7"),sQuery(id+"F0.wireOp",EDGE,"E6.2.0"),sQuery(id+"F0.wireOp",EDGE,"E6.2.4"),sQuery(id+"F0.wireOp",EDGE,"E6.2.5"),sQuery(id+"F0.wireOp",EDGE,"E6.2.6"),sQuery(id+"F0.wireOp",EDGE,"E6.2.7"),sQuery(id+"F0.wireOp",EDGE,"E6.3.0"),sQuery(id+"F0.wireOp",EDGE,"E6.3.4"),sQuery(id+"F0.wireOp",EDGE,"E6.3.5"),sQuery(id+"F0.wireOp",EDGE,"E6.3.6"),sQuery(id+"F0.wireOp",EDGE,"E6.3.7"),sQuery(id+"F0.wireOp",EDGE,"E6.4.0"),sQuery(id+"F0.wireOp",EDGE,"E6.4.4"),sQuery(id+"F0.wireOp",EDGE,"E6.4.5"),sQuery(id+"F0.wireOp",EDGE,"E6.4.6"),sQuery(id+"F0.wireOp",EDGE,"E6.4.7"),sQuery(id+"F0.wireOp",EDGE,"E6.5.0"),sQuery(id+"F0.wireOp",EDGE,"E6.5.4"),sQuery(id+"F0.wireOp",EDGE,"E6.5.5"),sQuery(id+"F0.wireOp",EDGE,"E6.5.6"),sQuery(id+"F0.wireOp",EDGE,"E6.5.7"),sQuery(id+"F0.wireOp",EDGE,"E6.6.0"),sQuery(id+"F0.wireOp",EDGE,"E6.6.4"),sQuery(id+"F0.wireOp",EDGE,"E6.6.5"),sQuery(id+"F0.wireOp",EDGE,"E6.6.6"),sQuery(id+"F0.wireOp",EDGE,"E6.6.7"),sQuery(id+"F0.wireOp",EDGE,"E6.7.0"),sQuery(id+"F0.wireOp",EDGE,"E6.7.4"),sQuery(id+"F0.wireOp",EDGE,"E6.7.5"),sQuery(id+"F0.wireOp",EDGE,"E6.7.6"),sQuery(id+"F0.wireOp",EDGE,"E6.7.7"),sQuery(id+"F0.wireOp",EDGE,"E6.8.0"),sQuery(id+"F0.wireOp",EDGE,"E6.8.4"),sQuery(id+"F0.wireOp",EDGE,"E6.8.5"),sQuery(id+"F0.wireOp",EDGE,"E6.8.6"),sQuery(id+"F0.wireOp",EDGE,"E6.8.7"),sQuery(id+"F0.wireOp",EDGE,"E6.9.0"),sQuery(id+"F0.wireOp",EDGE,"E6.9.4"),sQuery(id+"F0.wireOp",EDGE,"E6.9.5"),sQuery(id+"F0.wireOp",EDGE,"E6.9.6"),sQuery(id+"F0.wireOp",EDGE,"E6.9.7"),sQuery(id+"F0.wireOp",EDGE,"E6.10.0"),sQuery(id+"F0.wireOp",EDGE,"E6.10.4"),sQuery(id+"F0.wireOp",EDGE,"E6.10.5"),sQuery(id+"F0.wireOp",EDGE,"E6.10.6"),sQuery(id+"F0.wireOp",EDGE,"E6.10.7"),sQuery(id+"F0.wireOp",EDGE,"E6.11.0"),sQuery(id+"F0.wireOp",EDGE,"E6.11.4"),sQuery(id+"F0.wireOp",EDGE,"E6.11.5"),sQuery(id+"F0.wireOp",EDGE,"E6.11.6"),sQuery(id+"F0.wireOp",EDGE,"E6.11.7"),sQuery(id+"F0.wireOp",EDGE,"E6.12.0"),sQuery(id+"F0.wireOp",EDGE,"E6.12.4"),sQuery(id+"F0.wireOp",EDGE,"E6.12.5"),sQuery(id+"F0.wireOp",EDGE,"E6.12.6"),sQuery(id+"F0.wireOp",EDGE,"E6.12.7"),sQuery(id+"F0.wireOp",EDGE,"E6.13.0"),sQuery(id+"F0.wireOp",EDGE,"E6.13.4"),sQuery(id+"F0.wireOp",EDGE,"E6.13.5"),sQuery(id+"F0.wireOp",EDGE,"E6.13.6"),sQuery(id+"F0.wireOp",EDGE,"E6.13.7"),sQuery(id+"F0.wireOp",EDGE,"E6.14.0"),sQuery(id+"F0.wireOp",EDGE,"E6.14.4"),sQuery(id+"F0.wireOp",EDGE,"E6.14.5"),sQuery(id+"F0.wireOp",EDGE,"E6.14.6"),sQuery(id+"F0.wireOp",EDGE,"E6.14.7"),sQuery(id+"F0.wireOp",EDGE,"E6.15.0"),sQuery(id+"F0.wireOp",EDGE,"E6.15.4"),sQuery(id+"F0.wireOp",EDGE,"E6.15.5"),sQuery(id+"F0.wireOp",EDGE,"E6.15.6"),sQuery(id+"F0.wireOp",EDGE,"E6.15.7"),sQuery(id+"F0.wireOp",EDGE,"E6.16.0"),sQuery(id+"F0.wireOp",EDGE,"E6.16.4"),sQuery(id+"F0.wireOp",EDGE,"E6.16.5"),sQuery(id+"F0.wireOp",EDGE,"E6.16.6"),sQuery(id+"F0.wireOp",EDGE,"E6.16.7"),sQuery(id+"F0.wireOp",EDGE,"E6.17.0"),sQuery(id+"F0.wireOp",EDGE,"E6.17.4"),sQuery(id+"F0.wireOp",EDGE,"E6.17.5"),sQuery(id+"F0.wireOp",EDGE,"E6.17.6"),sQuery(id+"F0.wireOp",EDGE,"E6.17.7"),sQuery(id+"F0.wireOp",EDGE,"E6.18.0"),sQuery(id+"F0.wireOp",EDGE,"E6.18.4"),sQuery(id+"F0.wireOp",EDGE,"E6.18.5"),sQuery(id+"F0.wireOp",EDGE,"E6.18.6"),sQuery(id+"F0.wireOp",EDGE,"E6.18.7"),sQuery(id+"F0.wireOp",EDGE,"E6.19.0"),sQuery(id+"F0.wireOp",EDGE,"E6.19.4"),sQuery(id+"F0.wireOp",EDGE,"E6.19.5"),sQuery(id+"F0.wireOp",EDGE,"E6.19.6"),sQuery(id+"F0.wireOp",EDGE,"E6.19.7"),sQuery(id+"F0.wireOp",EDGE,"E6.20.0"),sQuery(id+"F0.wireOp",EDGE,"E6.20.4"),sQuery(id+"F0.wireOp",EDGE,"E6.20.5"),sQuery(id+"F0.wireOp",EDGE,"E6.20.6"),sQuery(id+"F0.wireOp",EDGE,"E6.20.7"),sQuery(id+"F0.wireOp",EDGE,"E6.21.0"),sQuery(id+"F0.wireOp",EDGE,"E6.21.4"),sQuery(id+"F0.wireOp",EDGE,"E6.21.5"),sQuery(id+"F0.wireOp",EDGE,"E6.21.6"),sQuery(id+"F0.wireOp",EDGE,"E6.21.7"),sQuery(id+"F0.wireOp",EDGE,"E6.22.0"),sQuery(id+"F0.wireOp",EDGE,"E6.22.4"),sQuery(id+"F0.wireOp",EDGE,"E6.22.5"),sQuery(id+"F0.wireOp",EDGE,"E6.22.6"),sQuery(id+"F0.wireOp",EDGE,"E6.22.7"),sQuery(id+"F0.wireOp",EDGE,"E6.23.0"),sQuery(id+"F0.wireOp",EDGE,"E6.23.4"),sQuery(id+"F0.wireOp",EDGE,"E6.23.5"),sQuery(id+"F0.wireOp",EDGE,"E6.23.6"),sQuery(id+"F0.wireOp",EDGE,"E6.23.7"),sQuery(id+"F0.wireOp",EDGE,"E6.24.0"),sQuery(id+"F0.wireOp",EDGE,"E6.24.4"),sQuery(id+"F0.wireOp",EDGE,"E6.24.5"),sQuery(id+"F0.wireOp",EDGE,"E6.24.6"),sQuery(id+"F0.wireOp",EDGE,"E6.24.7"),sQuery(id+"F0.wireOp",EDGE,"E6.25.0"),sQuery(id+"F0.wireOp",EDGE,"E6.25.4"),sQuery(id+"F0.wireOp",EDGE,"E6.25.5"),sQuery(id+"F0.wireOp",EDGE,"E6.25.6"),sQuery(id+"F0.wireOp",EDGE,"E6.25.7"),sQuery(id+"F0.wireOp",EDGE,"E6.26.0"),sQuery(id+"F0.wireOp",EDGE,"E6.26.4"),sQuery(id+"F0.wireOp",EDGE,"E6.26.5"),sQuery(id+"F0.wireOp",EDGE,"E6.26.6"),sQuery(id+"F0.wireOp",EDGE,"E6.26.7"),sQuery(id+"F0.wireOp",EDGE,"E6.27.0"),sQuery(id+"F0.wireOp",EDGE,"E6.27.4"),sQuery(id+"F0.wireOp",EDGE,"E6.27.5"),sQuery(id+"F0.wireOp",EDGE,"E6.27.6"),sQuery(id+"F0.wireOp",EDGE,"E6.27.7"),sQuery(id+"F0.wireOp",EDGE,"E6.28.0"),sQuery(id+"F0.wireOp",EDGE,"E6.28.4"),sQuery(id+"F0.wireOp",EDGE,"E6.28.5"),sQuery(id+"F0.wireOp",EDGE,"E6.28.6"),sQuery(id+"F0.wireOp",EDGE,"E6.28.7"),sQuery(id+"F0.wireOp",EDGE,"E6.29.0"),sQuery(id+"F0.wireOp",EDGE,"E6.29.4"),sQuery(id+"F0.wireOp",EDGE,"E6.29.5"),sQuery(id+"F0.wireOp",EDGE,"E6.29.6"),sQuery(id+"F0.wireOp",EDGE,"E6.29.7"),sQuery(id+"F0.wireOp",EDGE,"E6.30.0"),sQuery(id+"F0.wireOp",EDGE,"E6.30.4"),sQuery(id+"F0.wireOp",EDGE,"E6.30.5"),sQuery(id+"F0.wireOp",EDGE,"E6.30.6"),sQuery(id+"F0.wireOp",EDGE,"E6.30.7"),sQuery(id+"F0.wireOp",EDGE,"E6.31.0"),sQuery(id+"F0.wireOp",EDGE,"E6.31.4"),sQuery(id+"F0.wireOp",EDGE,"E6.31.5"),sQuery(id+"F0.wireOp",EDGE,"E6.31.6"),sQuery(id+"F0.wireOp",EDGE,"E6.31.7"),sQuery(id+"F0.wireOp",EDGE,"E6.32.0"),sQuery(id+"F0.wireOp",EDGE,"E6.32.4"),sQuery(id+"F0.wireOp",EDGE,"E6.32.5"),sQuery(id+"F0.wireOp",EDGE,"E6.32.6"),sQuery(id+"F0.wireOp",EDGE,"E6.32.7"),sQuery(id+"F0.wireOp",EDGE,"E6.33.0"),sQuery(id+"F0.wireOp",EDGE,"E6.33.4"),sQuery(id+"F0.wireOp",EDGE,"E6.33.5"),sQuery(id+"F0.wireOp",EDGE,"E6.33.6"),sQuery(id+"F0.wireOp",EDGE,"E6.33.7"),sQuery(id+"F0.wireOp",EDGE,"E6.34.0"),sQuery(id+"F0.wireOp",EDGE,"E6.34.4"),sQuery(id+"F0.wireOp",EDGE,"E6.34.5"),sQuery(id+"F0.wireOp",EDGE,"E6.34.6"),sQuery(id+"F0.wireOp",EDGE,"E6.34.7"),sQuery(id+"F0.wireOp",EDGE,"E6.35.0"),sQuery(id+"F0.wireOp",EDGE,"E6.35.4"),sQuery(id+"F0.wireOp",EDGE,"E6.35.5"),sQuery(id+"F0.wireOp",EDGE,"E6.35.6"),sQuery(id+"F0.wireOp",EDGE,"E6.35.7"),sQuery(id+"F0.wireOp",EDGE,"E6.36.0"),sQuery(id+"F0.wireOp",EDGE,"E6.36.4"),sQuery(id+"F0.wireOp",EDGE,"E6.36.5"),sQuery(id+"F0.wireOp",EDGE,"E6.36.6"),sQuery(id+"F0.wireOp",EDGE,"E6.36.7"),sQuery(id+"F0.wireOp",EDGE,"E6.37.0"),sQuery(id+"F0.wireOp",EDGE,"E6.37.4"),sQuery(id+"F0.wireOp",EDGE,"E6.37.5"),sQuery(id+"F0.wireOp",EDGE,"E6.37.6"),sQuery(id+"F0.wireOp",EDGE,"E6.37.7"),sQuery(id+"F0.wireOp",EDGE,"E6.38.0"),sQuery(id+"F0.wireOp",EDGE,"E6.38.4"),sQuery(id+"F0.wireOp",EDGE,"E6.38.5"),sQuery(id+"F0.wireOp",EDGE,"E6.38.6"),sQuery(id+"F0.wireOp",EDGE,"E6.38.7"),sQuery(id+"F0.wireOp",EDGE,"E6.39.0"),sQuery(id+"F0.wireOp",EDGE,"E6.39.4"),sQuery(id+"F0.wireOp",EDGE,"E6.39.5"),sQuery(id+"F0.wireOp",EDGE,"E6.39.6"),sQuery(id+"F0.wireOp",EDGE,"E6.39.7"),sQuery(id+"F0.wireOp",EDGE,"E6.40.0"),sQuery(id+"F0.wireOp",EDGE,"E6.40.4"),sQuery(id+"F0.wireOp",EDGE,"E6.40.5"),sQuery(id+"F0.wireOp",EDGE,"E6.40.6"),sQuery(id+"F0.wireOp",EDGE,"E6.40.7"),sQuery(id+"F0.wireOp",EDGE,"E6.41.0"),sQuery(id+"F0.wireOp",EDGE,"E6.41.4"),sQuery(id+"F0.wireOp",EDGE,"E6.41.5"),sQuery(id+"F0.wireOp",EDGE,"E6.41.6"),sQuery(id+"F0.wireOp",EDGE,"E6.41.7"),sQuery(id+"F0.wireOp",EDGE,"E6.42.0"),sQuery(id+"F0.wireOp",EDGE,"E6.42.4"),sQuery(id+"F0.wireOp",EDGE,"E6.42.5"),sQuery(id+"F0.wireOp",EDGE,"E6.42.6"),sQuery(id+"F0.wireOp",EDGE,"E6.42.7"),sQuery(id+"F0.wireOp",EDGE,"E6.43.0"),sQuery(id+"F0.wireOp",EDGE,"E6.43.4"),sQuery(id+"F0.wireOp",EDGE,"E6.43.5"),sQuery(id+"F0.wireOp",EDGE,"E6.43.6"),sQuery(id+"F0.wireOp",EDGE,"E6.43.7"),sQuery(id+"F0.wireOp",EDGE,"E6.44.0"),sQuery(id+"F0.wireOp",EDGE,"E6.44.4"),sQuery(id+"F0.wireOp",EDGE,"E6.44.5"),sQuery(id+"F0.wireOp",EDGE,"E6.44.6"),sQuery(id+"F0.wireOp",EDGE,"E6.44.7"),sQuery(id+"F0.wireOp",EDGE,"E6.45.0"),sQuery(id+"F0.wireOp",EDGE,"E6.45.4"),sQuery(id+"F0.wireOp",EDGE,"E6.45.5"),sQuery(id+"F0.wireOp",EDGE,"E6.45.6"),sQuery(id+"F0.wireOp",EDGE,"E6.45.7"),sQuery(id+"F0.wireOp",EDGE,"E6.46.0"),sQuery(id+"F0.wireOp",EDGE,"E6.46.4"),sQuery(id+"F0.wireOp",EDGE,"E6.46.5"),sQuery(id+"F0.wireOp",EDGE,"E6.46.6"),sQuery(id+"F0.wireOp",EDGE,"E6.46.7"),sQuery(id+"F0.wireOp",EDGE,"E6.47.0"),sQuery(id+"F0.wireOp",EDGE,"E6.47.4"),sQuery(id+"F0.wireOp",EDGE,"E6.47.5"),sQuery(id+"F0.wireOp",EDGE,"E6.47.6"),sQuery(id+"F0.wireOp",EDGE,"E6.47.7"),sQuery(id+"F0.wireOp",EDGE,"E6.48.0"),sQuery(id+"F0.wireOp",EDGE,"E6.48.4"),sQuery(id+"F0.wireOp",EDGE,"E6.48.5"),sQuery(id+"F0.wireOp",EDGE,"E6.48.6"),sQuery(id+"F0.wireOp",EDGE,"E6.48.7"),sQuery(id+"F0.wireOp",EDGE,"E6.49.0"),sQuery(id+"F0.wireOp",EDGE,"E6.49.4"),sQuery(id+"F0.wireOp",EDGE,"E6.49.5"),sQuery(id+"F0.wireOp",EDGE,"E6.49.6"),sQuery(id+"F0.wireOp",EDGE,"E6.49.7")])],"isStart":true});
            fillet(context, id + "F8", {"entities" : qUnion([Q0]), "radius" : 1 * mm, "tangentPropagation" : true, "allowEdgeOverflow" : false});
        }
        {
            var Q0;
            Q0=makeQuery(id+"F7.boolean.opBoolean","MERGE",FACE,{"derivedFrom":[makeQuery(id+"F1.opExtrude","CAP_FACE",FACE,{"disambiguationData":[OSD([sQuery(id+"F0.wireOp",EDGE,"E0"),sQuery(id+"F0.wireOp",EDGE,"E1"),sQuery(id+"F0.wireOp",EDGE,"E2"),sQuery(id+"F0.wireOp",EDGE,"E3.filletArc"),sQuery(id+"F0.wireOp",EDGE,"E4.filletArc"),sQuery(id+"F0.wireOp",EDGE,"E6.1.0"),sQuery(id+"F0.wireOp",EDGE,"E6.1.4"),sQuery(id+"F0.wireOp",EDGE,"E6.1.5"),sQuery(id+"F0.wireOp",EDGE,"E6.1.6"),sQuery(id+"F0.wireOp",EDGE,"E6.1.7"),sQuery(id+"F0.wireOp",EDGE,"E6.2.0"),sQuery(id+"F0.wireOp",EDGE,"E6.2.4"),sQuery(id+"F0.wireOp",EDGE,"E6.2.5"),sQuery(id+"F0.wireOp",EDGE,"E6.2.6"),sQuery(id+"F0.wireOp",EDGE,"E6.2.7"),sQuery(id+"F0.wireOp",EDGE,"E6.3.0"),sQuery(id+"F0.wireOp",EDGE,"E6.3.4"),sQuery(id+"F0.wireOp",EDGE,"E6.3.5"),sQuery(id+"F0.wireOp",EDGE,"E6.3.6"),sQuery(id+"F0.wireOp",EDGE,"E6.3.7"),sQuery(id+"F0.wireOp",EDGE,"E6.4.0"),sQuery(id+"F0.wireOp",EDGE,"E6.4.4"),sQuery(id+"F0.wireOp",EDGE,"E6.4.5"),sQuery(id+"F0.wireOp",EDGE,"E6.4.6"),sQuery(id+"F0.wireOp",EDGE,"E6.4.7"),sQuery(id+"F0.wireOp",EDGE,"E6.5.0"),sQuery(id+"F0.wireOp",EDGE,"E6.5.4"),sQuery(id+"F0.wireOp",EDGE,"E6.5.5"),sQuery(id+"F0.wireOp",EDGE,"E6.5.6"),sQuery(id+"F0.wireOp",EDGE,"E6.5.7"),sQuery(id+"F0.wireOp",EDGE,"E6.6.0"),sQuery(id+"F0.wireOp",EDGE,"E6.6.4"),sQuery(id+"F0.wireOp",EDGE,"E6.6.5"),sQuery(id+"F0.wireOp",EDGE,"E6.6.6"),sQuery(id+"F0.wireOp",EDGE,"E6.6.7"),sQuery(id+"F0.wireOp",EDGE,"E6.7.0"),sQuery(id+"F0.wireOp",EDGE,"E6.7.4"),sQuery(id+"F0.wireOp",EDGE,"E6.7.5"),sQuery(id+"F0.wireOp",EDGE,"E6.7.6"),sQuery(id+"F0.wireOp",EDGE,"E6.7.7"),sQuery(id+"F0.wireOp",EDGE,"E6.8.0"),sQuery(id+"F0.wireOp",EDGE,"E6.8.4"),sQuery(id+"F0.wireOp",EDGE,"E6.8.5"),sQuery(id+"F0.wireOp",EDGE,"E6.8.6"),sQuery(id+"F0.wireOp",EDGE,"E6.8.7"),sQuery(id+"F0.wireOp",EDGE,"E6.9.0"),sQuery(id+"F0.wireOp",EDGE,"E6.9.4"),sQuery(id+"F0.wireOp",EDGE,"E6.9.5"),sQuery(id+"F0.wireOp",EDGE,"E6.9.6"),sQuery(id+"F0.wireOp",EDGE,"E6.9.7"),sQuery(id+"F0.wireOp",EDGE,"E6.10.0"),sQuery(id+"F0.wireOp",EDGE,"E6.10.4"),sQuery(id+"F0.wireOp",EDGE,"E6.10.5"),sQuery(id+"F0.wireOp",EDGE,"E6.10.6"),sQuery(id+"F0.wireOp",EDGE,"E6.10.7"),sQuery(id+"F0.wireOp",EDGE,"E6.11.0"),sQuery(id+"F0.wireOp",EDGE,"E6.11.4"),sQuery(id+"F0.wireOp",EDGE,"E6.11.5"),sQuery(id+"F0.wireOp",EDGE,"E6.11.6"),sQuery(id+"F0.wireOp",EDGE,"E6.11.7"),sQuery(id+"F0.wireOp",EDGE,"E6.12.0"),sQuery(id+"F0.wireOp",EDGE,"E6.12.4"),sQuery(id+"F0.wireOp",EDGE,"E6.12.5"),sQuery(id+"F0.wireOp",EDGE,"E6.12.6"),sQuery(id+"F0.wireOp",EDGE,"E6.12.7"),sQuery(id+"F0.wireOp",EDGE,"E6.13.0"),sQuery(id+"F0.wireOp",EDGE,"E6.13.4"),sQuery(id+"F0.wireOp",EDGE,"E6.13.5"),sQuery(id+"F0.wireOp",EDGE,"E6.13.6"),sQuery(id+"F0.wireOp",EDGE,"E6.13.7"),sQuery(id+"F0.wireOp",EDGE,"E6.14.0"),sQuery(id+"F0.wireOp",EDGE,"E6.14.4"),sQuery(id+"F0.wireOp",EDGE,"E6.14.5"),sQuery(id+"F0.wireOp",EDGE,"E6.14.6"),sQuery(id+"F0.wireOp",EDGE,"E6.14.7"),sQuery(id+"F0.wireOp",EDGE,"E6.15.0"),sQuery(id+"F0.wireOp",EDGE,"E6.15.4"),sQuery(id+"F0.wireOp",EDGE,"E6.15.5"),sQuery(id+"F0.wireOp",EDGE,"E6.15.6"),sQuery(id+"F0.wireOp",EDGE,"E6.15.7"),sQuery(id+"F0.wireOp",EDGE,"E6.16.0"),sQuery(id+"F0.wireOp",EDGE,"E6.16.4"),sQuery(id+"F0.wireOp",EDGE,"E6.16.5"),sQuery(id+"F0.wireOp",EDGE,"E6.16.6"),sQuery(id+"F0.wireOp",EDGE,"E6.16.7"),sQuery(id+"F0.wireOp",EDGE,"E6.17.0"),sQuery(id+"F0.wireOp",EDGE,"E6.17.4"),sQuery(id+"F0.wireOp",EDGE,"E6.17.5"),sQuery(id+"F0.wireOp",EDGE,"E6.17.6"),sQuery(id+"F0.wireOp",EDGE,"E6.17.7"),sQuery(id+"F0.wireOp",EDGE,"E6.18.0"),sQuery(id+"F0.wireOp",EDGE,"E6.18.4"),sQuery(id+"F0.wireOp",EDGE,"E6.18.5"),sQuery(id+"F0.wireOp",EDGE,"E6.18.6"),sQuery(id+"F0.wireOp",EDGE,"E6.18.7"),sQuery(id+"F0.wireOp",EDGE,"E6.19.0"),sQuery(id+"F0.wireOp",EDGE,"E6.19.4"),sQuery(id+"F0.wireOp",EDGE,"E6.19.5"),sQuery(id+"F0.wireOp",EDGE,"E6.19.6"),sQuery(id+"F0.wireOp",EDGE,"E6.19.7"),sQuery(id+"F0.wireOp",EDGE,"E6.20.0"),sQuery(id+"F0.wireOp",EDGE,"E6.20.4"),sQuery(id+"F0.wireOp",EDGE,"E6.20.5"),sQuery(id+"F0.wireOp",EDGE,"E6.20.6"),sQuery(id+"F0.wireOp",EDGE,"E6.20.7"),sQuery(id+"F0.wireOp",EDGE,"E6.21.0"),sQuery(id+"F0.wireOp",EDGE,"E6.21.4"),sQuery(id+"F0.wireOp",EDGE,"E6.21.5"),sQuery(id+"F0.wireOp",EDGE,"E6.21.6"),sQuery(id+"F0.wireOp",EDGE,"E6.21.7"),sQuery(id+"F0.wireOp",EDGE,"E6.22.0"),sQuery(id+"F0.wireOp",EDGE,"E6.22.4"),sQuery(id+"F0.wireOp",EDGE,"E6.22.5"),sQuery(id+"F0.wireOp",EDGE,"E6.22.6"),sQuery(id+"F0.wireOp",EDGE,"E6.22.7"),sQuery(id+"F0.wireOp",EDGE,"E6.23.0"),sQuery(id+"F0.wireOp",EDGE,"E6.23.4"),sQuery(id+"F0.wireOp",EDGE,"E6.23.5"),sQuery(id+"F0.wireOp",EDGE,"E6.23.6"),sQuery(id+"F0.wireOp",EDGE,"E6.23.7"),sQuery(id+"F0.wireOp",EDGE,"E6.24.0"),sQuery(id+"F0.wireOp",EDGE,"E6.24.4"),sQuery(id+"F0.wireOp",EDGE,"E6.24.5"),sQuery(id+"F0.wireOp",EDGE,"E6.24.6"),sQuery(id+"F0.wireOp",EDGE,"E6.24.7"),sQuery(id+"F0.wireOp",EDGE,"E6.25.0"),sQuery(id+"F0.wireOp",EDGE,"E6.25.4"),sQuery(id+"F0.wireOp",EDGE,"E6.25.5"),sQuery(id+"F0.wireOp",EDGE,"E6.25.6"),sQuery(id+"F0.wireOp",EDGE,"E6.25.7"),sQuery(id+"F0.wireOp",EDGE,"E6.26.0"),sQuery(id+"F0.wireOp",EDGE,"E6.26.4"),sQuery(id+"F0.wireOp",EDGE,"E6.26.5"),sQuery(id+"F0.wireOp",EDGE,"E6.26.6"),sQuery(id+"F0.wireOp",EDGE,"E6.26.7"),sQuery(id+"F0.wireOp",EDGE,"E6.27.0"),sQuery(id+"F0.wireOp",EDGE,"E6.27.4"),sQuery(id+"F0.wireOp",EDGE,"E6.27.5"),sQuery(id+"F0.wireOp",EDGE,"E6.27.6"),sQuery(id+"F0.wireOp",EDGE,"E6.27.7"),sQuery(id+"F0.wireOp",EDGE,"E6.28.0"),sQuery(id+"F0.wireOp",EDGE,"E6.28.4"),sQuery(id+"F0.wireOp",EDGE,"E6.28.5"),sQuery(id+"F0.wireOp",EDGE,"E6.28.6"),sQuery(id+"F0.wireOp",EDGE,"E6.28.7"),sQuery(id+"F0.wireOp",EDGE,"E6.29.0"),sQuery(id+"F0.wireOp",EDGE,"E6.29.4"),sQuery(id+"F0.wireOp",EDGE,"E6.29.5"),sQuery(id+"F0.wireOp",EDGE,"E6.29.6"),sQuery(id+"F0.wireOp",EDGE,"E6.29.7"),sQuery(id+"F0.wireOp",EDGE,"E6.30.0"),sQuery(id+"F0.wireOp",EDGE,"E6.30.4"),sQuery(id+"F0.wireOp",EDGE,"E6.30.5"),sQuery(id+"F0.wireOp",EDGE,"E6.30.6"),sQuery(id+"F0.wireOp",EDGE,"E6.30.7"),sQuery(id+"F0.wireOp",EDGE,"E6.31.0"),sQuery(id+"F0.wireOp",EDGE,"E6.31.4"),sQuery(id+"F0.wireOp",EDGE,"E6.31.5"),sQuery(id+"F0.wireOp",EDGE,"E6.31.6"),sQuery(id+"F0.wireOp",EDGE,"E6.31.7"),sQuery(id+"F0.wireOp",EDGE,"E6.32.0"),sQuery(id+"F0.wireOp",EDGE,"E6.32.4"),sQuery(id+"F0.wireOp",EDGE,"E6.32.5"),sQuery(id+"F0.wireOp",EDGE,"E6.32.6"),sQuery(id+"F0.wireOp",EDGE,"E6.32.7"),sQuery(id+"F0.wireOp",EDGE,"E6.33.0"),sQuery(id+"F0.wireOp",EDGE,"E6.33.4"),sQuery(id+"F0.wireOp",EDGE,"E6.33.5"),sQuery(id+"F0.wireOp",EDGE,"E6.33.6"),sQuery(id+"F0.wireOp",EDGE,"E6.33.7"),sQuery(id+"F0.wireOp",EDGE,"E6.34.0"),sQuery(id+"F0.wireOp",EDGE,"E6.34.4"),sQuery(id+"F0.wireOp",EDGE,"E6.34.5"),sQuery(id+"F0.wireOp",EDGE,"E6.34.6"),sQuery(id+"F0.wireOp",EDGE,"E6.34.7"),sQuery(id+"F0.wireOp",EDGE,"E6.35.0"),sQuery(id+"F0.wireOp",EDGE,"E6.35.4"),sQuery(id+"F0.wireOp",EDGE,"E6.35.5"),sQuery(id+"F0.wireOp",EDGE,"E6.35.6"),sQuery(id+"F0.wireOp",EDGE,"E6.35.7"),sQuery(id+"F0.wireOp",EDGE,"E6.36.0"),sQuery(id+"F0.wireOp",EDGE,"E6.36.4"),sQuery(id+"F0.wireOp",EDGE,"E6.36.5"),sQuery(id+"F0.wireOp",EDGE,"E6.36.6"),sQuery(id+"F0.wireOp",EDGE,"E6.36.7"),sQuery(id+"F0.wireOp",EDGE,"E6.37.0"),sQuery(id+"F0.wireOp",EDGE,"E6.37.4"),sQuery(id+"F0.wireOp",EDGE,"E6.37.5"),sQuery(id+"F0.wireOp",EDGE,"E6.37.6"),sQuery(id+"F0.wireOp",EDGE,"E6.37.7"),sQuery(id+"F0.wireOp",EDGE,"E6.38.0"),sQuery(id+"F0.wireOp",EDGE,"E6.38.4"),sQuery(id+"F0.wireOp",EDGE,"E6.38.5"),sQuery(id+"F0.wireOp",EDGE,"E6.38.6"),sQuery(id+"F0.wireOp",EDGE,"E6.38.7"),sQuery(id+"F0.wireOp",EDGE,"E6.39.0"),sQuery(id+"F0.wireOp",EDGE,"E6.39.4"),sQuery(id+"F0.wireOp",EDGE,"E6.39.5"),sQuery(id+"F0.wireOp",EDGE,"E6.39.6"),sQuery(id+"F0.wireOp",EDGE,"E6.39.7"),sQuery(id+"F0.wireOp",EDGE,"E6.40.0"),sQuery(id+"F0.wireOp",EDGE,"E6.40.4"),sQuery(id+"F0.wireOp",EDGE,"E6.40.5"),sQuery(id+"F0.wireOp",EDGE,"E6.40.6"),sQuery(id+"F0.wireOp",EDGE,"E6.40.7"),sQuery(id+"F0.wireOp",EDGE,"E6.41.0"),sQuery(id+"F0.wireOp",EDGE,"E6.41.4"),sQuery(id+"F0.wireOp",EDGE,"E6.41.5"),sQuery(id+"F0.wireOp",EDGE,"E6.41.6"),sQuery(id+"F0.wireOp",EDGE,"E6.41.7"),sQuery(id+"F0.wireOp",EDGE,"E6.42.0"),sQuery(id+"F0.wireOp",EDGE,"E6.42.4"),sQuery(id+"F0.wireOp",EDGE,"E6.42.5"),sQuery(id+"F0.wireOp",EDGE,"E6.42.6"),sQuery(id+"F0.wireOp",EDGE,"E6.42.7"),sQuery(id+"F0.wireOp",EDGE,"E6.43.0"),sQuery(id+"F0.wireOp",EDGE,"E6.43.4"),sQuery(id+"F0.wireOp",EDGE,"E6.43.5"),sQuery(id+"F0.wireOp",EDGE,"E6.43.6"),sQuery(id+"F0.wireOp",EDGE,"E6.43.7"),sQuery(id+"F0.wireOp",EDGE,"E6.44.0"),sQuery(id+"F0.wireOp",EDGE,"E6.44.4"),sQuery(id+"F0.wireOp",EDGE,"E6.44.5"),sQuery(id+"F0.wireOp",EDGE,"E6.44.6"),sQuery(id+"F0.wireOp",EDGE,"E6.44.7"),sQuery(id+"F0.wireOp",EDGE,"E6.45.0"),sQuery(id+"F0.wireOp",EDGE,"E6.45.4"),sQuery(id+"F0.wireOp",EDGE,"E6.45.5"),sQuery(id+"F0.wireOp",EDGE,"E6.45.6"),sQuery(id+"F0.wireOp",EDGE,"E6.45.7"),sQuery(id+"F0.wireOp",EDGE,"E6.46.0"),sQuery(id+"F0.wireOp",EDGE,"E6.46.4"),sQuery(id+"F0.wireOp",EDGE,"E6.46.5"),sQuery(id+"F0.wireOp",EDGE,"E6.46.6"),sQuery(id+"F0.wireOp",EDGE,"E6.46.7"),sQuery(id+"F0.wireOp",EDGE,"E6.47.0"),sQuery(id+"F0.wireOp",EDGE,"E6.47.4"),sQuery(id+"F0.wireOp",EDGE,"E6.47.5"),sQuery(id+"F0.wireOp",EDGE,"E6.47.6"),sQuery(id+"F0.wireOp",EDGE,"E6.47.7"),sQuery(id+"F0.wireOp",EDGE,"E6.48.0"),sQuery(id+"F0.wireOp",EDGE,"E6.48.4"),sQuery(id+"F0.wireOp",EDGE,"E6.48.5"),sQuery(id+"F0.wireOp",EDGE,"E6.48.6"),sQuery(id+"F0.wireOp",EDGE,"E6.48.7"),sQuery(id+"F0.wireOp",EDGE,"E6.49.0"),sQuery(id+"F0.wireOp",EDGE,"E6.49.4"),sQuery(id+"F0.wireOp",EDGE,"E6.49.5"),sQuery(id+"F0.wireOp",EDGE,"E6.49.6"),sQuery(id+"F0.wireOp",EDGE,"E6.49.7")])],"isStart":false}),makeQuery(id+"F7.opExtrude","CAP_FACE",FACE,{"disambiguationData":[OSD([sQuery(id+"F6.wireOp",EDGE,"E16"),sQuery(id+"F6.wireOp",EDGE,"E17")])],"isStart":true})]});
            var sketch = newSketch(context, id + "F9", { "sketchPlane" : qUnion([Q0])});
            skArc(sketch, "E18", {"start": v(-11.52, -32.36) * mm, "mid": v(-5.85, -33.85) * mm, "end": v(0, -34.35) * mm});
            skLineSegment(sketch, "E19", {"start": v(0, -33.05) * mm, "end": v(0, 0) * mm});
            skLineSegment(sketch, "E20", {"start": v(-11.52, -32.36) * mm, "end": v(-11.09, -31.14) * mm});
            skLineSegment(sketch, "E21.MirrorCS", {"start": v(11.52, -32.36) * mm, "end": v(11.09, -31.14) * mm});
            skArc(sketch, "E22.MirrorCS", {"start": v(11.52, -32.36) * mm, "mid": v(5.85, -33.85) * mm, "end": v(0, -34.35) * mm});
            skLineSegment(sketch, "E23.1.0", {"start": v(32.36, -11.52) * mm, "end": v(31.14, -11.09) * mm});
            skArc(sketch, "E23.1.1", {"start": v(32.36, -11.52) * mm, "mid": v(33.85, -5.85) * mm, "end": v(34.35, 0) * mm});
            skArc(sketch, "E23.1.2", {"start": v(32.36, 11.52) * mm, "mid": v(33.85, 5.85) * mm, "end": v(34.35, 0) * mm});
            skLineSegment(sketch, "E23.1.3", {"start": v(32.36, 11.52) * mm, "end": v(31.14, 11.09) * mm});
            skLineSegment(sketch, "E23.2.0", {"start": v(11.52, 32.36) * mm, "end": v(11.09, 31.14) * mm});
            skArc(sketch, "E23.2.1", {"start": v(11.52, 32.36) * mm, "mid": v(5.85, 33.85) * mm, "end": v(0, 34.35) * mm});
            skArc(sketch, "E23.2.2", {"start": v(-11.52, 32.36) * mm, "mid": v(-5.85, 33.85) * mm, "end": v(0, 34.35) * mm});
            skLineSegment(sketch, "E23.2.3", {"start": v(-11.52, 32.36) * mm, "end": v(-11.09, 31.14) * mm});
            skLineSegment(sketch, "E23.3.0", {"start": v(-32.36, 11.52) * mm, "end": v(-31.14, 11.09) * mm});
            skArc(sketch, "E23.3.1", {"start": v(-32.36, 11.52) * mm, "mid": v(-33.85, 5.85) * mm, "end": v(-34.35, 0) * mm});
            skArc(sketch, "E23.3.2", {"start": v(-32.36, -11.52) * mm, "mid": v(-33.85, -5.85) * mm, "end": v(-34.35, 0) * mm});
            skLineSegment(sketch, "E23.3.3", {"start": v(-32.36, -11.52) * mm, "end": v(-31.14, -11.09) * mm});
            skSolve(sketch);
        }
        {
            var Q0;
            {var subQ1=sQuery(id+"F9.wireOp",EDGE,"E23.3.0");Q0=makeQuery(id+"F9.imprint","IMPRINT",FACE,{"disambiguationData":[TD([[makeQuery(id+"F9.imprint","IMPRINT",EDGE,{"derivedFrom":subQ1}),-1.0]])]});}
            var Q1;
            Q1=makeQuery(id+"F9.imprint","IMPRINT",FACE,{"disambiguationData":[TD([[makeQuery(id+"F9.imprint","IMPRINT",EDGE,{"derivedFrom":sQuery(id+"F9.wireOp",EDGE,"E18")}),1.0]])]});
            var Q2;
            {var subQ1=sQuery(id+"F9.wireOp",EDGE,"E23.1.0");Q2=makeQuery(id+"F9.imprint","IMPRINT",FACE,{"disambiguationData":[TD([[makeQuery(id+"F9.imprint","IMPRINT",EDGE,{"derivedFrom":subQ1}),-1.0]])]});}
            var Q3;
            {var subQ1=sQuery(id+"F9.wireOp",EDGE,"E23.2.0");Q3=makeQuery(id+"F9.imprint","IMPRINT",FACE,{"disambiguationData":[TD([[makeQuery(id+"F9.imprint","IMPRINT",EDGE,{"derivedFrom":subQ1}),-1.0]])]});}
            extrude(context, id + "F10", {"entities" : qUnion([Q0, Q1, Q2, Q3]), "operationType" : NewBodyOperationType.REMOVE, "oppositeDirection" : true, "depth" : 3 * mm});
        }
    });
